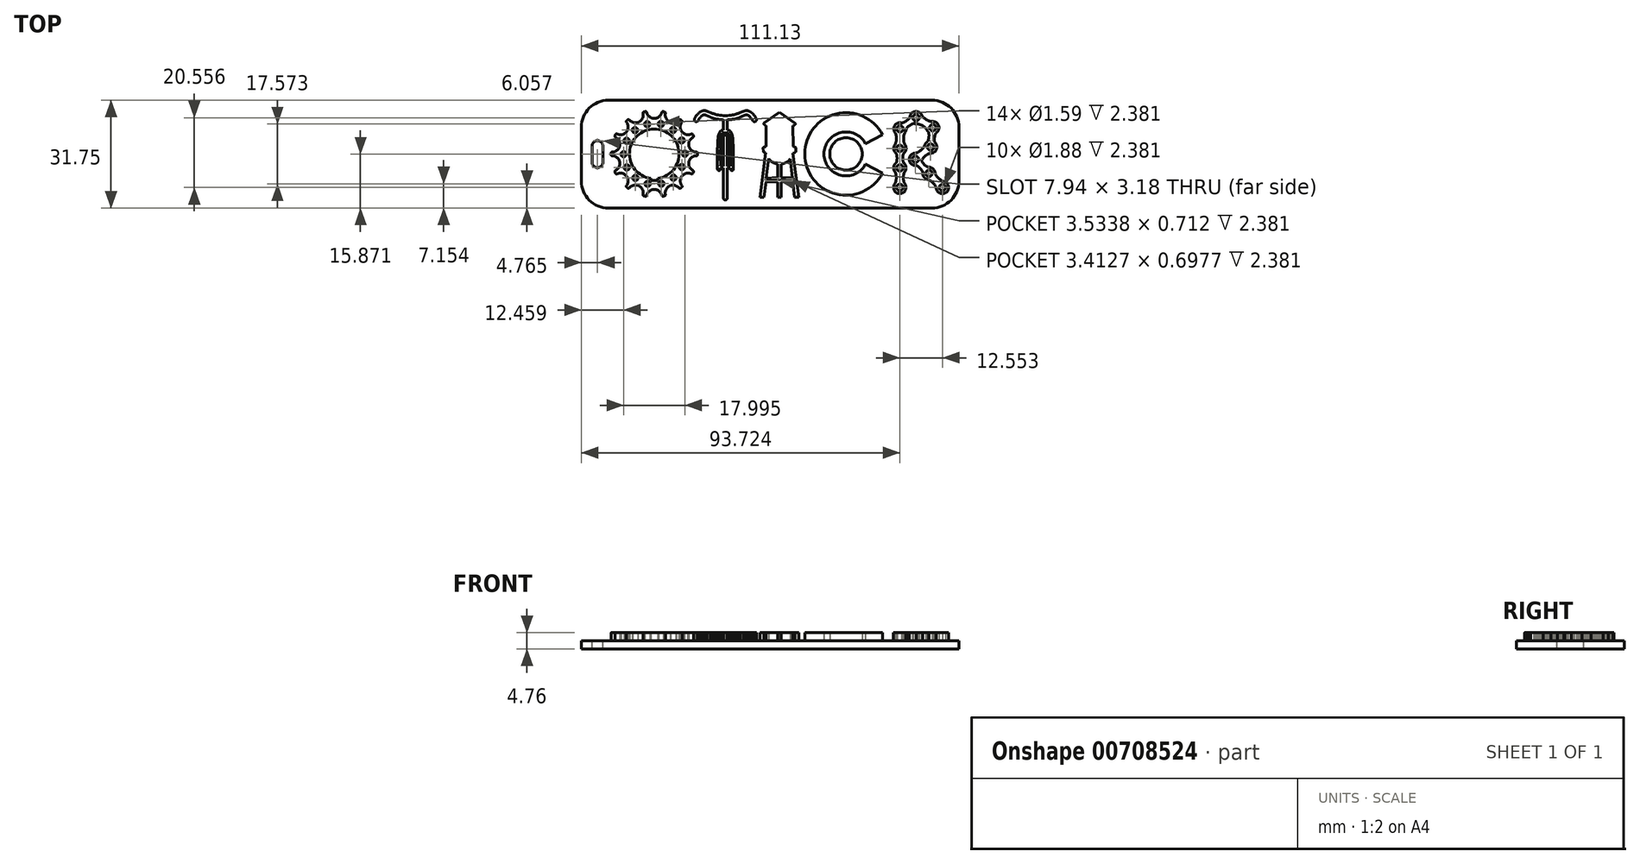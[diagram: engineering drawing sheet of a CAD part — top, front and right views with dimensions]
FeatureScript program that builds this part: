
annotation { "Feature Type Name" : "Feature", "Feature Type Description" : "" }
export const myFeature = defineFeature(function(context is Context, id is Id, definition is map)
    precondition{}
    {
        {
            var Q0;
            Q0=qCreatedBy(makeId("Top.planeOp"),FACE);
            var sketch = newSketch(context, id + "F0", { "sketchPlane" : qUnion([Q0])});
            skArc(sketch, "E0", {"start": v(-33.82, 12.73) * mm, "mid": v(-34.05, 12.78) * mm, "end": v(-34.28, 12.83) * mm});
            skArc(sketch, "E1", {"start": v(-33.6, 12.35) * mm, "mid": v(-33.63, 12.59) * mm, "end": v(-33.82, 12.73) * mm});
            skArc(sketch, "E2", {"start": v(-39.1, 12.6) * mm, "mid": v(-36.88, 10.82) * mm, "end": v(-34.66, 12.6) * mm});
            skArc(sketch, "E3", {"start": v(-34.28, 12.83) * mm, "mid": v(-34.52, 12.8) * mm, "end": v(-34.66, 12.6) * mm});
            skArc(sketch, "E4", {"start": v(-39.48, 12.83) * mm, "mid": v(-39.71, 12.78) * mm, "end": v(-39.94, 12.73) * mm});
            skArc(sketch, "E5", {"start": v(-39.1, 12.6) * mm, "mid": v(-39.25, 12.8) * mm, "end": v(-39.48, 12.83) * mm});
            skArc(sketch, "E6", {"start": v(-44.19, 10.42) * mm, "mid": v(-41.41, 9.79) * mm, "end": v(-40.18, 12.35) * mm});
            skArc(sketch, "E7", {"start": v(-39.94, 12.73) * mm, "mid": v(-40.14, 12.59) * mm, "end": v(-40.18, 12.35) * mm});
            skArc(sketch, "E8", {"start": v(-44.63, 10.47) * mm, "mid": v(-44.82, 10.33) * mm, "end": v(-45, 10.18) * mm});
            skArc(sketch, "E9", {"start": v(-44.19, 10.42) * mm, "mid": v(-44.4, 10.54) * mm, "end": v(-44.63, 10.47) * mm});
            skArc(sketch, "E10", {"start": v(-47.82, 6.26) * mm, "mid": v(-45.04, 6.89) * mm, "end": v(-45.04, 9.74) * mm});
            skArc(sketch, "E11", {"start": v(-45, 10.18) * mm, "mid": v(-45.11, 9.97) * mm, "end": v(-45.04, 9.74) * mm});
            skArc(sketch, "E12", {"start": v(-48.24, 6.11) * mm, "mid": v(-48.35, 5.9) * mm, "end": v(-48.45, 5.69) * mm});
            skArc(sketch, "E13", {"start": v(-47.82, 6.26) * mm, "mid": v(-48.06, 6.27) * mm, "end": v(-48.24, 6.11) * mm});
            skArc(sketch, "E14", {"start": v(-49.29, 0.93) * mm, "mid": v(-47.06, 2.7) * mm, "end": v(-48.3, 5.27) * mm});
            skArc(sketch, "E15", {"start": v(-48.45, 5.69) * mm, "mid": v(-48.46, 5.45) * mm, "end": v(-48.3, 5.27) * mm});
            skArc(sketch, "E16", {"start": v(-49.6, 0.62) * mm, "mid": v(-49.6, 0.38) * mm, "end": v(-49.6, 0.15) * mm});
            skArc(sketch, "E17", {"start": v(-49.29, 0.93) * mm, "mid": v(-49.5, 0.84) * mm, "end": v(-49.6, 0.62) * mm});
            skArc(sketch, "E18", {"start": v(-48.3, -4.5) * mm, "mid": v(-47.06, -1.94) * mm, "end": v(-49.29, -0.17) * mm});
            skArc(sketch, "E19", {"start": v(-49.6, 0.15) * mm, "mid": v(-49.5, -0.08) * mm, "end": v(-49.29, -0.17) * mm});
            skArc(sketch, "E20", {"start": v(-48.45, -4.93) * mm, "mid": v(-48.35, -5.14) * mm, "end": v(-48.24, -5.35) * mm});
            skArc(sketch, "E21", {"start": v(-48.3, -4.5) * mm, "mid": v(-48.46, -4.69) * mm, "end": v(-48.45, -4.93) * mm});
            skArc(sketch, "E22", {"start": v(-45.04, -8.97) * mm, "mid": v(-45.04, -6.13) * mm, "end": v(-47.82, -5.5) * mm});
            skArc(sketch, "E23", {"start": v(-48.24, -5.35) * mm, "mid": v(-48.06, -5.5) * mm, "end": v(-47.82, -5.5) * mm});
            skArc(sketch, "E24", {"start": v(-45, -9.42) * mm, "mid": v(-44.82, -9.57) * mm, "end": v(-44.63, -9.71) * mm});
            skArc(sketch, "E25", {"start": v(-45.04, -8.97) * mm, "mid": v(-45.11, -9.2) * mm, "end": v(-45, -9.42) * mm});
            skArc(sketch, "E26", {"start": v(-40.18, -11.59) * mm, "mid": v(-41.41, -9.02) * mm, "end": v(-44.19, -9.66) * mm});
            skArc(sketch, "E27", {"start": v(-44.63, -9.71) * mm, "mid": v(-44.4, -9.77) * mm, "end": v(-44.19, -9.66) * mm});
            skArc(sketch, "E28", {"start": v(-39.94, -11.97) * mm, "mid": v(-39.71, -12.02) * mm, "end": v(-39.48, -12.07) * mm});
            skArc(sketch, "E29", {"start": v(-40.18, -11.59) * mm, "mid": v(-40.14, -11.83) * mm, "end": v(-39.94, -11.97) * mm});
            skArc(sketch, "E30", {"start": v(-34.66, -11.83) * mm, "mid": v(-36.88, -10.06) * mm, "end": v(-39.1, -11.83) * mm});
            skArc(sketch, "E31", {"start": v(-39.48, -12.07) * mm, "mid": v(-39.25, -12.03) * mm, "end": v(-39.1, -11.83) * mm});
            skArc(sketch, "E32", {"start": v(-34.28, -12.07) * mm, "mid": v(-34.05, -12.02) * mm, "end": v(-33.82, -11.97) * mm});
            skArc(sketch, "E33", {"start": v(-34.66, -11.83) * mm, "mid": v(-34.52, -12.03) * mm, "end": v(-34.28, -12.07) * mm});
            skArc(sketch, "E34", {"start": v(-29.58, -9.66) * mm, "mid": v(-32.35, -9.02) * mm, "end": v(-33.6, -11.59) * mm});
            skArc(sketch, "E35", {"start": v(-33.82, -11.97) * mm, "mid": v(-33.63, -11.83) * mm, "end": v(-33.6, -11.59) * mm});
            skArc(sketch, "E36", {"start": v(-29.14, -9.71) * mm, "mid": v(-28.95, -9.57) * mm, "end": v(-28.77, -9.42) * mm});
            skArc(sketch, "E37", {"start": v(-29.58, -9.66) * mm, "mid": v(-29.37, -9.77) * mm, "end": v(-29.14, -9.71) * mm});
            skArc(sketch, "E38", {"start": v(-25.95, -5.5) * mm, "mid": v(-28.72, -6.13) * mm, "end": v(-28.72, -8.97) * mm});
            skArc(sketch, "E39", {"start": v(-28.77, -9.42) * mm, "mid": v(-28.66, -9.2) * mm, "end": v(-28.72, -8.97) * mm});
            skArc(sketch, "E40", {"start": v(-25.52, -5.35) * mm, "mid": v(-25.42, -5.14) * mm, "end": v(-25.32, -4.93) * mm});
            skArc(sketch, "E41", {"start": v(-25.95, -5.5) * mm, "mid": v(-25.7, -5.5) * mm, "end": v(-25.52, -5.35) * mm});
            skArc(sketch, "E42", {"start": v(-24.48, -0.17) * mm, "mid": v(-26.7, -1.94) * mm, "end": v(-25.47, -4.5) * mm});
            skArc(sketch, "E43", {"start": v(-25.32, -4.93) * mm, "mid": v(-25.31, -4.69) * mm, "end": v(-25.47, -4.5) * mm});
            skArc(sketch, "E44", {"start": v(-24.16, 0.15) * mm, "mid": v(-24.16, 0.38) * mm, "end": v(-24.16, 0.62) * mm});
            skArc(sketch, "E45", {"start": v(-24.48, -0.17) * mm, "mid": v(-24.26, -0.08) * mm, "end": v(-24.16, 0.15) * mm});
            skArc(sketch, "E46", {"start": v(-25.47, 5.27) * mm, "mid": v(-26.7, 2.7) * mm, "end": v(-24.48, 0.93) * mm});
            skArc(sketch, "E47", {"start": v(-24.16, 0.62) * mm, "mid": v(-24.26, 0.84) * mm, "end": v(-24.48, 0.93) * mm});
            skArc(sketch, "E48", {"start": v(-25.32, 5.69) * mm, "mid": v(-25.42, 5.9) * mm, "end": v(-25.52, 6.11) * mm});
            skArc(sketch, "E49", {"start": v(-25.47, 5.27) * mm, "mid": v(-25.31, 5.45) * mm, "end": v(-25.32, 5.69) * mm});
            skArc(sketch, "E50", {"start": v(-28.72, 9.74) * mm, "mid": v(-28.72, 6.89) * mm, "end": v(-25.95, 6.26) * mm});
            skArc(sketch, "E51", {"start": v(-25.52, 6.11) * mm, "mid": v(-25.7, 6.27) * mm, "end": v(-25.95, 6.26) * mm});
            skArc(sketch, "E52", {"start": v(-28.77, 10.18) * mm, "mid": v(-28.95, 10.33) * mm, "end": v(-29.14, 10.47) * mm});
            skArc(sketch, "E53", {"start": v(-28.72, 9.74) * mm, "mid": v(-28.66, 9.97) * mm, "end": v(-28.77, 10.18) * mm});
            skArc(sketch, "E54", {"start": v(-33.6, 12.35) * mm, "mid": v(-32.35, 9.79) * mm, "end": v(-29.58, 10.42) * mm});
            skArc(sketch, "E55", {"start": v(-29.14, 10.47) * mm, "mid": v(-29.37, 10.54) * mm, "end": v(-29.58, 10.42) * mm});
            skArc(sketch, "E56", {"start": v(-35.84, -6.84) * mm, "mid": v(-36.88, 7.68) * mm, "end": v(-37.93, -6.84) * mm});
            skCircle(sketch, "E57", {"center": v(19.55, 0.38) * mm, "radius": 4.78 * mm});
            skLineSegment(sketch, "E58", {"start": v(25.28, 3.4) * mm, "end": v(30.31, 6.04) * mm});
            skArc(sketch, "E59", {"start": v(30.31, 6.04) * mm, "mid": v(7.4, 0.38) * mm, "end": v(30.31, -5.28) * mm});
            skLineSegment(sketch, "E60", {"start": v(25.28, -2.63) * mm, "end": v(30.31, -5.28) * mm});
            skLineSegment(sketch, "E61", {"start": v(5.68, -12.44) * mm, "end": v(3.96, 0.55) * mm});
            skLineSegment(sketch, "E62", {"start": v(4.46, -12.44) * mm, "end": v(3.92, -7.7) * mm});
            skLineSegment(sketch, "E63", {"start": v(3.84, -7.32) * mm, "end": v(3.8, -7) * mm});
            skLineSegment(sketch, "E64", {"start": v(3.8, -6.65) * mm, "end": v(3.17, -1.11) * mm});
            skLineSegment(sketch, "E65", {"start": v(-0.06, 12.66) * mm, "end": v(4.72, 9.38) * mm});
            skLineSegment(sketch, "E66", {"start": v(-4.57, 9.45) * mm, "end": v(-0.06, 12.66) * mm});
            skLineSegment(sketch, "E67", {"start": v(3.92, -7.7) * mm, "end": v(0.42, -7.91) * mm});
            skLineSegment(sketch, "E68", {"start": v(-0.52, -7.9) * mm, "end": v(-4.03, -7.78) * mm});
            skLineSegment(sketch, "E69", {"start": v(-3.93, -6.74) * mm, "end": v(-0.52, -6.5) * mm});
            skLineSegment(sketch, "E70", {"start": v(0.42, -6.52) * mm, "end": v(3.8, -6.65) * mm});
            skLineSegment(sketch, "E71", {"start": v(3.84, -7.32) * mm, "end": v(0.42, -7.6) * mm});
            skLineSegment(sketch, "E72", {"start": v(-0.52, -7.54) * mm, "end": v(-4.05, -7.42) * mm});
            skLineSegment(sketch, "E73", {"start": v(-4.05, -7.42) * mm, "end": v(-3.98, -7.09) * mm});
            skLineSegment(sketch, "E74", {"start": v(-3.98, -7.09) * mm, "end": v(-0.52, -6.83) * mm});
            skLineSegment(sketch, "E75", {"start": v(0.42, -6.9) * mm, "end": v(3.8, -7) * mm});
            skLineSegment(sketch, "E76", {"start": v(3.94, 8.66) * mm, "end": v(4.02, 2.56) * mm});
            skLineSegment(sketch, "E77", {"start": v(-3.97, 8.65) * mm, "end": v(-3.96, 2.58) * mm});
            skLineSegment(sketch, "E78", {"start": v(4.85, 2.2) * mm, "end": v(4.82, 1.03) * mm});
            skLineSegment(sketch, "E79", {"start": v(-4.82, 2.22) * mm, "end": v(-4.8, 1) * mm});
            skArc(sketch, "E80", {"start": v(3.94, 8.66) * mm, "mid": v(4.44, 8.9) * mm, "end": v(4.72, 9.38) * mm});
            skArc(sketch, "E81", {"start": v(-4.57, 9.45) * mm, "mid": v(-4.44, 8.92) * mm, "end": v(-3.97, 8.65) * mm});
            skArc(sketch, "E82", {"start": v(4.85, 2.2) * mm, "mid": v(4.45, 2.43) * mm, "end": v(4.02, 2.56) * mm});
            skArc(sketch, "E83", {"start": v(-3.96, 2.58) * mm, "mid": v(-4.4, 2.44) * mm, "end": v(-4.82, 2.22) * mm});
            skArc(sketch, "E84", {"start": v(-4.8, 1) * mm, "mid": v(-4.43, 0.83) * mm, "end": v(-4.05, 0.7) * mm});
            skArc(sketch, "E85", {"start": v(3.96, 0.55) * mm, "mid": v(4.42, 0.74) * mm, "end": v(4.82, 1.03) * mm});
            skArc(sketch, "E86", {"start": v(-3.27, -0.99) * mm, "mid": v(-2.06, -2.07) * mm, "end": v(-0.52, -2.6) * mm});
            skArc(sketch, "E87", {"start": v(0.42, -2.6) * mm, "mid": v(1.94, -2.13) * mm, "end": v(3.17, -1.11) * mm});
            skLineSegment(sketch, "E88", {"start": v(-5.8, -12.44) * mm, "end": v(-4.05, 0.7) * mm});
            skLineSegment(sketch, "E89", {"start": v(-3.93, -6.74) * mm, "end": v(-3.27, -0.99) * mm});
            skLineSegment(sketch, "E90", {"start": v(-4.56, -12.44) * mm, "end": v(-4.03, -7.78) * mm});
            skLineSegment(sketch, "E91", {"start": v(-0.52, -2.6) * mm, "end": v(-0.52, -6.5) * mm});
            skLineSegment(sketch, "E92", {"start": v(-0.52, -7.9) * mm, "end": v(-0.52, -12.44) * mm});
            skLineSegment(sketch, "E93", {"start": v(0.42, -2.6) * mm, "end": v(0.42, -6.52) * mm});
            skLineSegment(sketch, "E94", {"start": v(0.42, -7.91) * mm, "end": v(0.42, -12.44) * mm});
            skLineSegment(sketch, "E95", {"start": v(-4.56, -12.44) * mm, "end": v(-5.8, -12.44) * mm});
            skLineSegment(sketch, "E96", {"start": v(0.42, -12.44) * mm, "end": v(-0.52, -12.44) * mm});
            skLineSegment(sketch, "E97", {"start": v(5.68, -12.44) * mm, "end": v(4.46, -12.44) * mm});
            skLineSegment(sketch, "E98", {"start": v(-15.95, 11.62) * mm, "end": v(-16.55, 11.66) * mm});
            skLineSegment(sketch, "E99", {"start": v(-16.55, 11.66) * mm, "end": v(-17.09, 11.7) * mm});
            skLineSegment(sketch, "E100", {"start": v(-17.09, 11.7) * mm, "end": v(-17.58, 11.77) * mm});
            skLineSegment(sketch, "E101", {"start": v(-17.58, 11.77) * mm, "end": v(-18.03, 11.84) * mm});
            skLineSegment(sketch, "E102", {"start": v(-18.03, 11.84) * mm, "end": v(-18.44, 11.93) * mm});
            skLineSegment(sketch, "E103", {"start": v(-18.44, 11.93) * mm, "end": v(-18.8, 12.02) * mm});
            skLineSegment(sketch, "E104", {"start": v(-18.8, 12.02) * mm, "end": v(-19.14, 12.1) * mm});
            skLineSegment(sketch, "E105", {"start": v(-19.14, 12.1) * mm, "end": v(-19.45, 12.2) * mm});
            skLineSegment(sketch, "E106", {"start": v(-19.45, 12.2) * mm, "end": v(-19.73, 12.3) * mm});
            skLineSegment(sketch, "E107", {"start": v(-19.73, 12.3) * mm, "end": v(-19.98, 12.39) * mm});
            skLineSegment(sketch, "E108", {"start": v(-19.98, 12.39) * mm, "end": v(-20.22, 12.48) * mm});
            skLineSegment(sketch, "E109", {"start": v(-20.22, 12.48) * mm, "end": v(-20.43, 12.56) * mm});
            skLineSegment(sketch, "E110", {"start": v(-20.43, 12.56) * mm, "end": v(-20.62, 12.64) * mm});
            skLineSegment(sketch, "E111", {"start": v(-20.62, 12.64) * mm, "end": v(-20.79, 12.72) * mm});
            skLineSegment(sketch, "E112", {"start": v(-20.79, 12.72) * mm, "end": v(-20.94, 12.78) * mm});
            skLineSegment(sketch, "E113", {"start": v(-20.94, 12.78) * mm, "end": v(-21.08, 12.85) * mm});
            skLineSegment(sketch, "E114", {"start": v(-21.08, 12.85) * mm, "end": v(-21.2, 12.9) * mm});
            skLineSegment(sketch, "E115", {"start": v(-21.2, 12.9) * mm, "end": v(-21.32, 12.95) * mm});
            skLineSegment(sketch, "E116", {"start": v(-21.32, 12.95) * mm, "end": v(-21.43, 12.98) * mm});
            skLineSegment(sketch, "E117", {"start": v(-21.43, 12.98) * mm, "end": v(-21.52, 13.02) * mm});
            skLineSegment(sketch, "E118", {"start": v(-21.52, 13.02) * mm, "end": v(-21.61, 13.05) * mm});
            skLineSegment(sketch, "E119", {"start": v(-21.61, 13.05) * mm, "end": v(-21.7, 13.07) * mm});
            skLineSegment(sketch, "E120", {"start": v(-21.7, 13.07) * mm, "end": v(-21.77, 13.09) * mm});
            skLineSegment(sketch, "E121", {"start": v(-21.77, 13.09) * mm, "end": v(-21.85, 13.1) * mm});
            skLineSegment(sketch, "E122", {"start": v(-21.85, 13.1) * mm, "end": v(-21.93, 13.11) * mm});
            skLineSegment(sketch, "E123", {"start": v(-21.93, 13.11) * mm, "end": v(-22, 13.12) * mm});
            skLineSegment(sketch, "E124", {"start": v(-22, 13.12) * mm, "end": v(-22.08, 13.13) * mm});
            skLineSegment(sketch, "E125", {"start": v(-22.08, 13.13) * mm, "end": v(-22.15, 13.13) * mm});
            skLineSegment(sketch, "E126", {"start": v(-22.15, 13.13) * mm, "end": v(-22.23, 13.13) * mm});
            skLineSegment(sketch, "E127", {"start": v(-22.23, 13.13) * mm, "end": v(-22.3, 13.12) * mm});
            skLineSegment(sketch, "E128", {"start": v(-22.3, 13.12) * mm, "end": v(-22.38, 13.11) * mm});
            skLineSegment(sketch, "E129", {"start": v(-22.38, 13.11) * mm, "end": v(-22.46, 13.1) * mm});
            skLineSegment(sketch, "E130", {"start": v(-22.46, 13.1) * mm, "end": v(-22.54, 13.09) * mm});
            skLineSegment(sketch, "E131", {"start": v(-22.54, 13.09) * mm, "end": v(-22.63, 13.07) * mm});
            skLineSegment(sketch, "E132", {"start": v(-22.63, 13.07) * mm, "end": v(-22.7, 13.04) * mm});
            skLineSegment(sketch, "E133", {"start": v(-22.7, 13.04) * mm, "end": v(-22.8, 13.02) * mm});
            skLineSegment(sketch, "E134", {"start": v(-22.8, 13.02) * mm, "end": v(-22.88, 12.99) * mm});
            skLineSegment(sketch, "E135", {"start": v(-22.88, 12.99) * mm, "end": v(-22.97, 12.95) * mm});
            skLineSegment(sketch, "E136", {"start": v(-22.97, 12.95) * mm, "end": v(-23.05, 12.91) * mm});
            skLineSegment(sketch, "E137", {"start": v(-23.05, 12.91) * mm, "end": v(-23.14, 12.87) * mm});
            skLineSegment(sketch, "E138", {"start": v(-23.14, 12.87) * mm, "end": v(-23.23, 12.82) * mm});
            skLineSegment(sketch, "E139", {"start": v(-23.23, 12.82) * mm, "end": v(-23.31, 12.77) * mm});
            skLineSegment(sketch, "E140", {"start": v(-23.31, 12.77) * mm, "end": v(-23.4, 12.72) * mm});
            skLineSegment(sketch, "E141", {"start": v(-23.4, 12.72) * mm, "end": v(-23.48, 12.66) * mm});
            skLineSegment(sketch, "E142", {"start": v(-23.48, 12.66) * mm, "end": v(-23.57, 12.6) * mm});
            skLineSegment(sketch, "E143", {"start": v(-23.57, 12.6) * mm, "end": v(-23.65, 12.53) * mm});
            skLineSegment(sketch, "E144", {"start": v(-23.65, 12.53) * mm, "end": v(-23.73, 12.47) * mm});
            skLineSegment(sketch, "E145", {"start": v(-23.73, 12.47) * mm, "end": v(-23.82, 12.4) * mm});
            skLineSegment(sketch, "E146", {"start": v(-23.82, 12.4) * mm, "end": v(-23.9, 12.32) * mm});
            skLineSegment(sketch, "E147", {"start": v(-23.9, 12.32) * mm, "end": v(-23.97, 12.25) * mm});
            skLineSegment(sketch, "E148", {"start": v(-23.97, 12.25) * mm, "end": v(-24.05, 12.17) * mm});
            skLineSegment(sketch, "E149", {"start": v(-24.05, 12.17) * mm, "end": v(-24.13, 12.08) * mm});
            skLineSegment(sketch, "E150", {"start": v(-24.13, 12.08) * mm, "end": v(-24.2, 12) * mm});
            skLineSegment(sketch, "E151", {"start": v(-24.2, 12) * mm, "end": v(-24.29, 11.9) * mm});
            skLineSegment(sketch, "E152", {"start": v(-24.29, 11.9) * mm, "end": v(-24.37, 11.8) * mm});
            skLineSegment(sketch, "E153", {"start": v(-24.37, 11.8) * mm, "end": v(-24.45, 11.69) * mm});
            skLineSegment(sketch, "E154", {"start": v(-24.45, 11.69) * mm, "end": v(-24.53, 11.57) * mm});
            skLineSegment(sketch, "E155", {"start": v(-24.53, 11.57) * mm, "end": v(-24.61, 11.45) * mm});
            skLineSegment(sketch, "E156", {"start": v(-24.61, 11.45) * mm, "end": v(-24.7, 11.33) * mm});
            skLineSegment(sketch, "E157", {"start": v(-24.7, 11.33) * mm, "end": v(-24.77, 11.2) * mm});
            skLineSegment(sketch, "E158", {"start": v(-24.77, 11.2) * mm, "end": v(-24.84, 11.08) * mm});
            skLineSegment(sketch, "E159", {"start": v(-24.84, 11.08) * mm, "end": v(-24.9, 10.96) * mm});
            skLineSegment(sketch, "E160", {"start": v(-24.9, 10.96) * mm, "end": v(-24.97, 10.85) * mm});
            skLineSegment(sketch, "E161", {"start": v(-24.97, 10.85) * mm, "end": v(-25.01, 10.74) * mm});
            skLineSegment(sketch, "E162", {"start": v(-25.01, 10.74) * mm, "end": v(-25.05, 10.65) * mm});
            skLineSegment(sketch, "E163", {"start": v(-25.05, 10.65) * mm, "end": v(-25.08, 10.57) * mm});
            skLineSegment(sketch, "E164", {"start": v(-25.08, 10.57) * mm, "end": v(-25.1, 10.5) * mm});
            skLineSegment(sketch, "E165", {"start": v(-25.1, 10.5) * mm, "end": v(-25.1, 10.43) * mm});
            skLineSegment(sketch, "E166", {"start": v(-25.1, 10.43) * mm, "end": v(-25.1, 10.38) * mm});
            skLineSegment(sketch, "E167", {"start": v(-25.1, 10.38) * mm, "end": v(-25.1, 10.32) * mm});
            skLineSegment(sketch, "E168", {"start": v(-25.1, 10.32) * mm, "end": v(-25.08, 10.27) * mm});
            skLineSegment(sketch, "E169", {"start": v(-25.08, 10.27) * mm, "end": v(-25.06, 10.23) * mm});
            skLineSegment(sketch, "E170", {"start": v(-25.06, 10.23) * mm, "end": v(-25.04, 10.18) * mm});
            skLineSegment(sketch, "E171", {"start": v(-25.04, 10.18) * mm, "end": v(-25, 10.14) * mm});
            skLineSegment(sketch, "E172", {"start": v(-25, 10.14) * mm, "end": v(-24.98, 10.1) * mm});
            skLineSegment(sketch, "E173", {"start": v(-24.98, 10.1) * mm, "end": v(-24.94, 10.06) * mm});
            skLineSegment(sketch, "E174", {"start": v(-24.94, 10.06) * mm, "end": v(-24.9, 10.03) * mm});
            skLineSegment(sketch, "E175", {"start": v(-24.9, 10.03) * mm, "end": v(-24.87, 10) * mm});
            skLineSegment(sketch, "E176", {"start": v(-24.87, 10) * mm, "end": v(-24.82, 9.97) * mm});
            skLineSegment(sketch, "E177", {"start": v(-24.82, 9.97) * mm, "end": v(-24.78, 9.94) * mm});
            skLineSegment(sketch, "E178", {"start": v(-24.78, 9.94) * mm, "end": v(-24.73, 9.92) * mm});
            skLineSegment(sketch, "E179", {"start": v(-24.73, 9.92) * mm, "end": v(-24.68, 9.9) * mm});
            skLineSegment(sketch, "E180", {"start": v(-24.68, 9.9) * mm, "end": v(-24.64, 9.9) * mm});
            skLineSegment(sketch, "E181", {"start": v(-24.64, 9.9) * mm, "end": v(-24.59, 9.89) * mm});
            skLineSegment(sketch, "E182", {"start": v(-24.59, 9.89) * mm, "end": v(-24.54, 9.89) * mm});
            skLineSegment(sketch, "E183", {"start": v(-24.54, 9.89) * mm, "end": v(-24.49, 9.89) * mm});
            skLineSegment(sketch, "E184", {"start": v(-24.49, 9.89) * mm, "end": v(-24.44, 9.89) * mm});
            skLineSegment(sketch, "E185", {"start": v(-24.44, 9.89) * mm, "end": v(-24.4, 9.9) * mm});
            skLineSegment(sketch, "E186", {"start": v(-24.4, 9.9) * mm, "end": v(-24.35, 9.9) * mm});
            skLineSegment(sketch, "E187", {"start": v(-24.35, 9.9) * mm, "end": v(-24.3, 9.92) * mm});
            skLineSegment(sketch, "E188", {"start": v(-24.3, 9.92) * mm, "end": v(-24.26, 9.94) * mm});
            skLineSegment(sketch, "E189", {"start": v(-24.26, 9.94) * mm, "end": v(-24.22, 9.96) * mm});
            skLineSegment(sketch, "E190", {"start": v(-24.22, 9.96) * mm, "end": v(-24.18, 9.99) * mm});
            skLineSegment(sketch, "E191", {"start": v(-24.18, 9.99) * mm, "end": v(-24.14, 10.02) * mm});
            skLineSegment(sketch, "E192", {"start": v(-24.14, 10.02) * mm, "end": v(-24.1, 10.06) * mm});
            skLineSegment(sketch, "E193", {"start": v(-24.1, 10.06) * mm, "end": v(-24.06, 10.1) * mm});
            skLineSegment(sketch, "E194", {"start": v(-24.06, 10.1) * mm, "end": v(-24.02, 10.16) * mm});
            skLineSegment(sketch, "E195", {"start": v(-24.02, 10.16) * mm, "end": v(-23.97, 10.22) * mm});
            skLineSegment(sketch, "E196", {"start": v(-23.97, 10.22) * mm, "end": v(-23.93, 10.28) * mm});
            skLineSegment(sketch, "E197", {"start": v(-23.93, 10.28) * mm, "end": v(-23.88, 10.35) * mm});
            skLineSegment(sketch, "E198", {"start": v(-23.88, 10.35) * mm, "end": v(-23.83, 10.43) * mm});
            skLineSegment(sketch, "E199", {"start": v(-23.83, 10.43) * mm, "end": v(-23.78, 10.5) * mm});
            skLineSegment(sketch, "E200", {"start": v(-23.78, 10.5) * mm, "end": v(-23.72, 10.59) * mm});
            skLineSegment(sketch, "E201", {"start": v(-23.72, 10.59) * mm, "end": v(-23.66, 10.67) * mm});
            skLineSegment(sketch, "E202", {"start": v(-23.66, 10.67) * mm, "end": v(-23.6, 10.76) * mm});
            skLineSegment(sketch, "E203", {"start": v(-23.6, 10.76) * mm, "end": v(-23.54, 10.86) * mm});
            skLineSegment(sketch, "E204", {"start": v(-23.54, 10.86) * mm, "end": v(-23.47, 10.95) * mm});
            skLineSegment(sketch, "E205", {"start": v(-23.47, 10.95) * mm, "end": v(-23.4, 11.04) * mm});
            skLineSegment(sketch, "E206", {"start": v(-23.4, 11.04) * mm, "end": v(-23.32, 11.13) * mm});
            skLineSegment(sketch, "E207", {"start": v(-23.32, 11.13) * mm, "end": v(-23.24, 11.22) * mm});
            skLineSegment(sketch, "E208", {"start": v(-23.24, 11.22) * mm, "end": v(-23.17, 11.3) * mm});
            skLineSegment(sketch, "E209", {"start": v(-23.17, 11.3) * mm, "end": v(-23.1, 11.39) * mm});
            skLineSegment(sketch, "E210", {"start": v(-23.1, 11.39) * mm, "end": v(-23.01, 11.46) * mm});
            skLineSegment(sketch, "E211", {"start": v(-23.01, 11.46) * mm, "end": v(-22.94, 11.53) * mm});
            skLineSegment(sketch, "E212", {"start": v(-22.94, 11.53) * mm, "end": v(-22.86, 11.6) * mm});
            skLineSegment(sketch, "E213", {"start": v(-22.86, 11.6) * mm, "end": v(-22.78, 11.65) * mm});
            skLineSegment(sketch, "E214", {"start": v(-22.78, 11.65) * mm, "end": v(-22.7, 11.7) * mm});
            skLineSegment(sketch, "E215", {"start": v(-22.7, 11.7) * mm, "end": v(-22.64, 11.75) * mm});
            skLineSegment(sketch, "E216", {"start": v(-22.64, 11.75) * mm, "end": v(-22.57, 11.79) * mm});
            skLineSegment(sketch, "E217", {"start": v(-22.57, 11.79) * mm, "end": v(-22.5, 11.82) * mm});
            skLineSegment(sketch, "E218", {"start": v(-22.5, 11.82) * mm, "end": v(-22.44, 11.85) * mm});
            skLineSegment(sketch, "E219", {"start": v(-22.44, 11.85) * mm, "end": v(-22.37, 11.87) * mm});
            skLineSegment(sketch, "E220", {"start": v(-22.37, 11.87) * mm, "end": v(-22.31, 11.88) * mm});
            skLineSegment(sketch, "E221", {"start": v(-22.31, 11.88) * mm, "end": v(-22.26, 11.9) * mm});
            skLineSegment(sketch, "E222", {"start": v(-22.26, 11.9) * mm, "end": v(-22.2, 11.9) * mm});
            skLineSegment(sketch, "E223", {"start": v(-22.2, 11.9) * mm, "end": v(-22.14, 11.9) * mm});
            skLineSegment(sketch, "E224", {"start": v(-22.14, 11.9) * mm, "end": v(-22.09, 11.9) * mm});
            skLineSegment(sketch, "E225", {"start": v(-22.09, 11.9) * mm, "end": v(-22.03, 11.89) * mm});
            skLineSegment(sketch, "E226", {"start": v(-22.03, 11.89) * mm, "end": v(-21.97, 11.88) * mm});
            skLineSegment(sketch, "E227", {"start": v(-21.97, 11.88) * mm, "end": v(-21.92, 11.87) * mm});
            skLineSegment(sketch, "E228", {"start": v(-21.92, 11.87) * mm, "end": v(-21.85, 11.85) * mm});
            skLineSegment(sketch, "E229", {"start": v(-21.85, 11.85) * mm, "end": v(-21.79, 11.83) * mm});
            skLineSegment(sketch, "E230", {"start": v(-21.79, 11.83) * mm, "end": v(-21.72, 11.81) * mm});
            skLineSegment(sketch, "E231", {"start": v(-21.72, 11.81) * mm, "end": v(-21.64, 11.78) * mm});
            skLineSegment(sketch, "E232", {"start": v(-21.64, 11.78) * mm, "end": v(-21.56, 11.75) * mm});
            skLineSegment(sketch, "E233", {"start": v(-21.56, 11.75) * mm, "end": v(-21.47, 11.7) * mm});
            skLineSegment(sketch, "E234", {"start": v(-21.47, 11.7) * mm, "end": v(-21.36, 11.66) * mm});
            skLineSegment(sketch, "E235", {"start": v(-21.36, 11.66) * mm, "end": v(-21.25, 11.61) * mm});
            skLineSegment(sketch, "E236", {"start": v(-21.25, 11.61) * mm, "end": v(-21.14, 11.56) * mm});
            skLineSegment(sketch, "E237", {"start": v(-21.14, 11.56) * mm, "end": v(-21.01, 11.5) * mm});
            skLineSegment(sketch, "E238", {"start": v(-21.01, 11.5) * mm, "end": v(-20.88, 11.44) * mm});
            skLineSegment(sketch, "E239", {"start": v(-20.88, 11.44) * mm, "end": v(-20.75, 11.38) * mm});
            skLineSegment(sketch, "E240", {"start": v(-20.75, 11.38) * mm, "end": v(-20.61, 11.31) * mm});
            skLineSegment(sketch, "E241", {"start": v(-20.61, 11.31) * mm, "end": v(-20.48, 11.25) * mm});
            skLineSegment(sketch, "E242", {"start": v(-20.48, 11.25) * mm, "end": v(-20.34, 11.2) * mm});
            skLineSegment(sketch, "E243", {"start": v(-20.34, 11.2) * mm, "end": v(-20.2, 11.13) * mm});
            skLineSegment(sketch, "E244", {"start": v(-20.2, 11.13) * mm, "end": v(-20.06, 11.08) * mm});
            skLineSegment(sketch, "E245", {"start": v(-20.06, 11.08) * mm, "end": v(-19.92, 11.02) * mm});
            skLineSegment(sketch, "E246", {"start": v(-19.92, 11.02) * mm, "end": v(-19.78, 10.97) * mm});
            skLineSegment(sketch, "E247", {"start": v(-19.78, 10.97) * mm, "end": v(-19.63, 10.92) * mm});
            skLineSegment(sketch, "E248", {"start": v(-19.63, 10.92) * mm, "end": v(-19.49, 10.87) * mm});
            skLineSegment(sketch, "E249", {"start": v(-19.49, 10.87) * mm, "end": v(-19.34, 10.82) * mm});
            skLineSegment(sketch, "E250", {"start": v(-19.34, 10.82) * mm, "end": v(-19.2, 10.78) * mm});
            skLineSegment(sketch, "E251", {"start": v(-19.2, 10.78) * mm, "end": v(-19.04, 10.74) * mm});
            skLineSegment(sketch, "E252", {"start": v(-19.04, 10.74) * mm, "end": v(-18.89, 10.7) * mm});
            skLineSegment(sketch, "E253", {"start": v(-18.89, 10.7) * mm, "end": v(-18.73, 10.67) * mm});
            skLineSegment(sketch, "E254", {"start": v(-18.73, 10.67) * mm, "end": v(-18.56, 10.64) * mm});
            skLineSegment(sketch, "E255", {"start": v(-18.56, 10.64) * mm, "end": v(-18.38, 10.6) * mm});
            skLineSegment(sketch, "E256", {"start": v(-18.38, 10.6) * mm, "end": v(-18.2, 10.58) * mm});
            skLineSegment(sketch, "E257", {"start": v(-18.2, 10.58) * mm, "end": v(-18, 10.55) * mm});
            skLineSegment(sketch, "E258", {"start": v(-18, 10.55) * mm, "end": v(-17.8, 10.52) * mm});
            skLineSegment(sketch, "E259", {"start": v(-17.8, 10.52) * mm, "end": v(-17.58, 10.5) * mm});
            skLineSegment(sketch, "E260", {"start": v(-17.58, 10.5) * mm, "end": v(-17.36, 10.48) * mm});
            skLineSegment(sketch, "E261", {"start": v(-17.36, 10.48) * mm, "end": v(-17.15, 10.46) * mm});
            skLineSegment(sketch, "E262", {"start": v(-17.15, 10.46) * mm, "end": v(-16.96, 10.44) * mm});
            skLineSegment(sketch, "E263", {"start": v(-16.96, 10.44) * mm, "end": v(-16.78, 10.43) * mm});
            skLineSegment(sketch, "E264", {"start": v(-16.78, 10.43) * mm, "end": v(-16.63, 10.42) * mm});
            skLineSegment(sketch, "E265", {"start": v(-16.63, 10.42) * mm, "end": v(-16.5, 10.42) * mm});
            skLineSegment(sketch, "E266", {"start": v(-16.5, -12.68) * mm, "end": v(-16.5, -3.7) * mm});
            skLineSegment(sketch, "E267", {"start": v(-16.5, -3.7) * mm, "end": v(-17.39, -3.7) * mm});
            skLineSegment(sketch, "E268", {"start": v(-17.39, -3.7) * mm, "end": v(-17.4, -3.85) * mm});
            skLineSegment(sketch, "E269", {"start": v(-17.4, -3.85) * mm, "end": v(-17.4, -4.05) * mm});
            skLineSegment(sketch, "E270", {"start": v(-17.4, -4.05) * mm, "end": v(-17.43, -4.19) * mm});
            skLineSegment(sketch, "E271", {"start": v(-17.43, -4.19) * mm, "end": v(-17.45, -4.29) * mm});
            skLineSegment(sketch, "E272", {"start": v(-17.45, -4.29) * mm, "end": v(-17.48, -4.35) * mm});
            skLineSegment(sketch, "E273", {"start": v(-17.48, -4.35) * mm, "end": v(-17.5, -4.39) * mm});
            skLineSegment(sketch, "E274", {"start": v(-17.5, -4.39) * mm, "end": v(-17.54, -4.41) * mm});
            skLineSegment(sketch, "E275", {"start": v(-17.54, -4.41) * mm, "end": v(-17.57, -4.43) * mm});
            skLineSegment(sketch, "E276", {"start": v(-17.57, -4.43) * mm, "end": v(-17.6, -4.45) * mm});
            skLineSegment(sketch, "E277", {"start": v(-17.6, -4.45) * mm, "end": v(-17.64, -4.47) * mm});
            skLineSegment(sketch, "E278", {"start": v(-17.64, -4.47) * mm, "end": v(-17.68, -4.48) * mm});
            skLineSegment(sketch, "E279", {"start": v(-17.68, -4.48) * mm, "end": v(-17.72, -4.5) * mm});
            skLineSegment(sketch, "E280", {"start": v(-17.72, -4.5) * mm, "end": v(-17.76, -4.5) * mm});
            skLineSegment(sketch, "E281", {"start": v(-17.76, -4.5) * mm, "end": v(-17.8, -4.5) * mm});
            skLineSegment(sketch, "E282", {"start": v(-17.8, -4.5) * mm, "end": v(-17.85, -4.5) * mm});
            skLineSegment(sketch, "E283", {"start": v(-17.85, -4.5) * mm, "end": v(-17.89, -4.5) * mm});
            skLineSegment(sketch, "E284", {"start": v(-17.89, -4.5) * mm, "end": v(-17.93, -4.5) * mm});
            skLineSegment(sketch, "E285", {"start": v(-17.93, -4.5) * mm, "end": v(-17.97, -4.48) * mm});
            skLineSegment(sketch, "E286", {"start": v(-17.97, -4.48) * mm, "end": v(-18.01, -4.47) * mm});
            skLineSegment(sketch, "E287", {"start": v(-18.01, -4.47) * mm, "end": v(-18.05, -4.46) * mm});
            skLineSegment(sketch, "E288", {"start": v(-18.05, -4.46) * mm, "end": v(-18.09, -4.44) * mm});
            skLineSegment(sketch, "E289", {"start": v(-18.09, -4.44) * mm, "end": v(-18.12, -4.42) * mm});
            skLineSegment(sketch, "E290", {"start": v(-18.12, -4.42) * mm, "end": v(-18.16, -4.4) * mm});
            skLineSegment(sketch, "E291", {"start": v(-18.16, -4.4) * mm, "end": v(-18.19, -4.37) * mm});
            skLineSegment(sketch, "E292", {"start": v(-18.19, -4.37) * mm, "end": v(-18.21, -4.34) * mm});
            skLineSegment(sketch, "E293", {"start": v(-18.21, -4.34) * mm, "end": v(-18.24, -4.28) * mm});
            skLineSegment(sketch, "E294", {"start": v(-18.24, -4.28) * mm, "end": v(-18.26, -4.2) * mm});
            skLineSegment(sketch, "E295", {"start": v(-18.26, -4.2) * mm, "end": v(-18.27, -4.1) * mm});
            skLineSegment(sketch, "E296", {"start": v(-18.27, -4.1) * mm, "end": v(-18.29, -3.94) * mm});
            skLineSegment(sketch, "E297", {"start": v(-18.29, -3.94) * mm, "end": v(-18.3, -3.74) * mm});
            skLineSegment(sketch, "E298", {"start": v(-18.3, -3.74) * mm, "end": v(-18.31, -3.48) * mm});
            skLineSegment(sketch, "E299", {"start": v(-18.31, -3.48) * mm, "end": v(-18.32, -3.16) * mm});
            skLineSegment(sketch, "E300", {"start": v(-18.32, -3.16) * mm, "end": v(-18.32, -2.79) * mm});
            skLineSegment(sketch, "E301", {"start": v(-18.32, -2.79) * mm, "end": v(-18.32, -2.36) * mm});
            skLineSegment(sketch, "E302", {"start": v(-18.32, -2.36) * mm, "end": v(-18.32, -1.9) * mm});
            skLineSegment(sketch, "E303", {"start": v(-18.32, -1.9) * mm, "end": v(-18.32, -1.4) * mm});
            skLineSegment(sketch, "E304", {"start": v(-18.32, -1.4) * mm, "end": v(-18.32, -0.87) * mm});
            skLineSegment(sketch, "E305", {"start": v(-18.32, -0.87) * mm, "end": v(-18.31, -0.33) * mm});
            skLineSegment(sketch, "E306", {"start": v(-18.31, -0.33) * mm, "end": v(-18.3, 0.23) * mm});
            skLineSegment(sketch, "E307", {"start": v(-18.3, 0.23) * mm, "end": v(-18.3, 0.8) * mm});
            skLineSegment(sketch, "E308", {"start": v(-18.3, 0.8) * mm, "end": v(-18.28, 1.35) * mm});
            skLineSegment(sketch, "E309", {"start": v(-18.28, 1.35) * mm, "end": v(-18.27, 1.9) * mm});
            skLineSegment(sketch, "E310", {"start": v(-18.27, 1.9) * mm, "end": v(-18.25, 2.45) * mm});
            skLineSegment(sketch, "E311", {"start": v(-18.25, 2.45) * mm, "end": v(-18.23, 2.97) * mm});
            skLineSegment(sketch, "E312", {"start": v(-18.23, 2.97) * mm, "end": v(-18.21, 3.46) * mm});
            skLineSegment(sketch, "E313", {"start": v(-18.21, 3.46) * mm, "end": v(-18.19, 3.92) * mm});
            skLineSegment(sketch, "E314", {"start": v(-18.19, 3.92) * mm, "end": v(-18.16, 4.35) * mm});
            skLineSegment(sketch, "E315", {"start": v(-18.16, 4.35) * mm, "end": v(-18.13, 4.73) * mm});
            skLineSegment(sketch, "E316", {"start": v(-18.13, 4.73) * mm, "end": v(-18.1, 5.07) * mm});
            skLineSegment(sketch, "E317", {"start": v(-18.1, 5.07) * mm, "end": v(-18.05, 5.37) * mm});
            skLineSegment(sketch, "E318", {"start": v(-18.05, 5.37) * mm, "end": v(-18.01, 5.64) * mm});
            skLineSegment(sketch, "E319", {"start": v(-18.01, 5.64) * mm, "end": v(-17.97, 5.87) * mm});
            skLineSegment(sketch, "E320", {"start": v(-17.97, 5.87) * mm, "end": v(-17.92, 6.08) * mm});
            skLineSegment(sketch, "E321", {"start": v(-17.92, 6.08) * mm, "end": v(-17.86, 6.27) * mm});
            skLineSegment(sketch, "E322", {"start": v(-17.86, 6.27) * mm, "end": v(-17.8, 6.43) * mm});
            skLineSegment(sketch, "E323", {"start": v(-17.8, 6.43) * mm, "end": v(-17.75, 6.58) * mm});
            skLineSegment(sketch, "E324", {"start": v(-17.75, 6.58) * mm, "end": v(-17.68, 6.7) * mm});
            skLineSegment(sketch, "E325", {"start": v(-17.68, 6.7) * mm, "end": v(-17.61, 6.82) * mm});
            skLineSegment(sketch, "E326", {"start": v(-17.61, 6.82) * mm, "end": v(-17.54, 6.93) * mm});
            skLineSegment(sketch, "E327", {"start": v(-17.54, 6.93) * mm, "end": v(-17.47, 7.02) * mm});
            skLineSegment(sketch, "E328", {"start": v(-17.47, 7.02) * mm, "end": v(-17.4, 7.1) * mm});
            skLineSegment(sketch, "E329", {"start": v(-17.4, 7.1) * mm, "end": v(-17.32, 7.16) * mm});
            skLineSegment(sketch, "E330", {"start": v(-17.32, 7.16) * mm, "end": v(-17.24, 7.22) * mm});
            skLineSegment(sketch, "E331", {"start": v(-17.24, 7.22) * mm, "end": v(-17.15, 7.28) * mm});
            skLineSegment(sketch, "E332", {"start": v(-17.15, 7.28) * mm, "end": v(-17.07, 7.32) * mm});
            skLineSegment(sketch, "E333", {"start": v(-17.07, 7.32) * mm, "end": v(-16.98, 7.36) * mm});
            skLineSegment(sketch, "E334", {"start": v(-16.98, 7.36) * mm, "end": v(-16.9, 7.4) * mm});
            skLineSegment(sketch, "E335", {"start": v(-16.9, 7.4) * mm, "end": v(-16.8, 7.42) * mm});
            skLineSegment(sketch, "E336", {"start": v(-16.8, 7.42) * mm, "end": v(-16.5, 7.48) * mm});
            skLineSegment(sketch, "E337", {"start": v(-16.5, 7.48) * mm, "end": v(-16.5, 10.42) * mm});
            skLineSegment(sketch, "E338", {"start": v(-16.16, 6.6) * mm, "end": v(-16.34, 6.6) * mm});
            skLineSegment(sketch, "E339", {"start": v(-16.34, 6.6) * mm, "end": v(-16.48, 6.59) * mm});
            skLineSegment(sketch, "E340", {"start": v(-16.48, 6.59) * mm, "end": v(-16.59, 6.57) * mm});
            skLineSegment(sketch, "E341", {"start": v(-16.59, 6.57) * mm, "end": v(-16.67, 6.55) * mm});
            skLineSegment(sketch, "E342", {"start": v(-16.67, 6.55) * mm, "end": v(-16.73, 6.53) * mm});
            skLineSegment(sketch, "E343", {"start": v(-16.73, 6.53) * mm, "end": v(-16.78, 6.5) * mm});
            skLineSegment(sketch, "E344", {"start": v(-16.78, 6.5) * mm, "end": v(-16.82, 6.47) * mm});
            skLineSegment(sketch, "E345", {"start": v(-16.82, 6.47) * mm, "end": v(-16.86, 6.44) * mm});
            skLineSegment(sketch, "E346", {"start": v(-16.86, 6.44) * mm, "end": v(-16.9, 6.4) * mm});
            skLineSegment(sketch, "E347", {"start": v(-16.9, 6.4) * mm, "end": v(-16.92, 6.37) * mm});
            skLineSegment(sketch, "E348", {"start": v(-16.92, 6.37) * mm, "end": v(-16.95, 6.32) * mm});
            skLineSegment(sketch, "E349", {"start": v(-16.95, 6.32) * mm, "end": v(-16.98, 6.27) * mm});
            skLineSegment(sketch, "E350", {"start": v(-16.98, 6.27) * mm, "end": v(-17, 6.22) * mm});
            skLineSegment(sketch, "E351", {"start": v(-17, 6.22) * mm, "end": v(-17.03, 6.16) * mm});
            skLineSegment(sketch, "E352", {"start": v(-17.03, 6.16) * mm, "end": v(-17.06, 6.1) * mm});
            skLineSegment(sketch, "E353", {"start": v(-17.06, 6.1) * mm, "end": v(-17.08, 6.01) * mm});
            skLineSegment(sketch, "E354", {"start": v(-17.08, 6.01) * mm, "end": v(-17.1, 5.93) * mm});
            skLineSegment(sketch, "E355", {"start": v(-17.1, 5.93) * mm, "end": v(-17.13, 5.82) * mm});
            skLineSegment(sketch, "E356", {"start": v(-17.13, 5.82) * mm, "end": v(-17.15, 5.7) * mm});
            skLineSegment(sketch, "E357", {"start": v(-17.15, 5.7) * mm, "end": v(-17.17, 5.54) * mm});
            skLineSegment(sketch, "E358", {"start": v(-17.17, 5.54) * mm, "end": v(-17.2, 5.35) * mm});
            skLineSegment(sketch, "E359", {"start": v(-17.2, 5.35) * mm, "end": v(-17.21, 5.13) * mm});
            skLineSegment(sketch, "E360", {"start": v(-17.21, 5.13) * mm, "end": v(-17.24, 4.87) * mm});
            skLineSegment(sketch, "E361", {"start": v(-17.24, 4.87) * mm, "end": v(-17.26, 4.57) * mm});
            skLineSegment(sketch, "E362", {"start": v(-17.26, 4.57) * mm, "end": v(-17.28, 4.22) * mm});
            skLineSegment(sketch, "E363", {"start": v(-17.28, 4.22) * mm, "end": v(-17.3, 3.83) * mm});
            skLineSegment(sketch, "E364", {"start": v(-17.3, 3.83) * mm, "end": v(-17.32, 3.4) * mm});
            skLineSegment(sketch, "E365", {"start": v(-17.32, 3.4) * mm, "end": v(-17.34, 2.93) * mm});
            skLineSegment(sketch, "E366", {"start": v(-17.34, 2.93) * mm, "end": v(-17.35, 2.42) * mm});
            skLineSegment(sketch, "E367", {"start": v(-17.35, 2.42) * mm, "end": v(-17.37, 1.88) * mm});
            skLineSegment(sketch, "E368", {"start": v(-17.37, 1.88) * mm, "end": v(-17.37, 1.3) * mm});
            skLineSegment(sketch, "E369", {"start": v(-17.37, 1.3) * mm, "end": v(-17.38, 0.7) * mm});
            skLineSegment(sketch, "E370", {"start": v(-17.38, 0.7) * mm, "end": v(-17.38, 0.07) * mm});
            skLineSegment(sketch, "E371", {"start": v(-17.38, 0.07) * mm, "end": v(-17.38, -0.57) * mm});
            skLineSegment(sketch, "E372", {"start": v(-17.38, -0.57) * mm, "end": v(-17.37, -1.18) * mm});
            skLineSegment(sketch, "E373", {"start": v(-17.37, -1.18) * mm, "end": v(-17.37, -1.78) * mm});
            skLineSegment(sketch, "E374", {"start": v(-17.37, -1.78) * mm, "end": v(-17.37, -2.33) * mm});
            skLineSegment(sketch, "E375", {"start": v(-17.37, -2.33) * mm, "end": v(-17.37, -2.82) * mm});
            skLineSegment(sketch, "E376", {"start": v(-17.37, -2.82) * mm, "end": v(-17.37, -3.28) * mm});
            skArc(sketch, "E377", {"start": v(-16.5, -12.68) * mm, "mid": v(-16.37, -13) * mm, "end": v(-16.06, -13.13) * mm});
            skLineSegment(sketch, "E378", {"start": v(-15.95, -13.13) * mm, "end": v(-16.06, -13.13) * mm});
            skArc(sketch, "E379", {"start": v(-16.06, 5.92) * mm, "mid": v(-16.37, 5.8) * mm, "end": v(-16.5, 5.48) * mm});
            skLineSegment(sketch, "E380", {"start": v(-16.5, -3.28) * mm, "end": v(-16.5, 5.48) * mm});
            skLineSegment(sketch, "E381", {"start": v(-15.95, 11.62) * mm, "end": v(-15.35, 11.66) * mm});
            skLineSegment(sketch, "E382", {"start": v(-15.35, 11.66) * mm, "end": v(-14.81, 11.7) * mm});
            skLineSegment(sketch, "E383", {"start": v(-14.81, 11.7) * mm, "end": v(-14.32, 11.77) * mm});
            skLineSegment(sketch, "E384", {"start": v(-14.32, 11.77) * mm, "end": v(-13.87, 11.84) * mm});
            skLineSegment(sketch, "E385", {"start": v(-13.87, 11.84) * mm, "end": v(-13.46, 11.93) * mm});
            skLineSegment(sketch, "E386", {"start": v(-13.46, 11.93) * mm, "end": v(-13.1, 12.02) * mm});
            skLineSegment(sketch, "E387", {"start": v(-13.1, 12.02) * mm, "end": v(-12.76, 12.1) * mm});
            skLineSegment(sketch, "E388", {"start": v(-12.76, 12.1) * mm, "end": v(-12.45, 12.2) * mm});
            skLineSegment(sketch, "E389", {"start": v(-12.45, 12.2) * mm, "end": v(-12.17, 12.3) * mm});
            skLineSegment(sketch, "E390", {"start": v(-12.17, 12.3) * mm, "end": v(-11.92, 12.39) * mm});
            skLineSegment(sketch, "E391", {"start": v(-11.92, 12.39) * mm, "end": v(-11.68, 12.48) * mm});
            skLineSegment(sketch, "E392", {"start": v(-11.68, 12.48) * mm, "end": v(-11.47, 12.56) * mm});
            skLineSegment(sketch, "E393", {"start": v(-11.47, 12.56) * mm, "end": v(-11.28, 12.64) * mm});
            skLineSegment(sketch, "E394", {"start": v(-11.28, 12.64) * mm, "end": v(-11.11, 12.72) * mm});
            skLineSegment(sketch, "E395", {"start": v(-11.11, 12.72) * mm, "end": v(-10.96, 12.78) * mm});
            skLineSegment(sketch, "E396", {"start": v(-10.96, 12.78) * mm, "end": v(-10.82, 12.85) * mm});
            skLineSegment(sketch, "E397", {"start": v(-10.82, 12.85) * mm, "end": v(-10.7, 12.9) * mm});
            skLineSegment(sketch, "E398", {"start": v(-10.7, 12.9) * mm, "end": v(-10.58, 12.95) * mm});
            skLineSegment(sketch, "E399", {"start": v(-10.58, 12.95) * mm, "end": v(-10.47, 12.98) * mm});
            skLineSegment(sketch, "E400", {"start": v(-10.47, 12.98) * mm, "end": v(-10.38, 13.02) * mm});
            skLineSegment(sketch, "E401", {"start": v(-10.38, 13.02) * mm, "end": v(-10.29, 13.05) * mm});
            skLineSegment(sketch, "E402", {"start": v(-10.29, 13.05) * mm, "end": v(-10.2, 13.07) * mm});
            skLineSegment(sketch, "E403", {"start": v(-10.2, 13.07) * mm, "end": v(-10.13, 13.09) * mm});
            skLineSegment(sketch, "E404", {"start": v(-10.13, 13.09) * mm, "end": v(-10.05, 13.1) * mm});
            skLineSegment(sketch, "E405", {"start": v(-10.05, 13.1) * mm, "end": v(-9.97, 13.11) * mm});
            skLineSegment(sketch, "E406", {"start": v(-9.97, 13.11) * mm, "end": v(-9.9, 13.12) * mm});
            skLineSegment(sketch, "E407", {"start": v(-9.9, 13.12) * mm, "end": v(-9.82, 13.13) * mm});
            skLineSegment(sketch, "E408", {"start": v(-9.82, 13.13) * mm, "end": v(-9.75, 13.13) * mm});
            skLineSegment(sketch, "E409", {"start": v(-9.75, 13.13) * mm, "end": v(-9.67, 13.13) * mm});
            skLineSegment(sketch, "E410", {"start": v(-9.67, 13.13) * mm, "end": v(-9.6, 13.12) * mm});
            skLineSegment(sketch, "E411", {"start": v(-9.6, 13.12) * mm, "end": v(-9.52, 13.11) * mm});
            skLineSegment(sketch, "E412", {"start": v(-9.52, 13.11) * mm, "end": v(-9.44, 13.1) * mm});
            skLineSegment(sketch, "E413", {"start": v(-9.44, 13.1) * mm, "end": v(-9.36, 13.09) * mm});
            skLineSegment(sketch, "E414", {"start": v(-9.36, 13.09) * mm, "end": v(-9.27, 13.07) * mm});
            skLineSegment(sketch, "E415", {"start": v(-9.27, 13.07) * mm, "end": v(-9.2, 13.04) * mm});
            skLineSegment(sketch, "E416", {"start": v(-9.2, 13.04) * mm, "end": v(-9.1, 13.02) * mm});
            skLineSegment(sketch, "E417", {"start": v(-9.1, 13.02) * mm, "end": v(-9.02, 12.99) * mm});
            skLineSegment(sketch, "E418", {"start": v(-9.02, 12.99) * mm, "end": v(-8.93, 12.95) * mm});
            skLineSegment(sketch, "E419", {"start": v(-8.93, 12.95) * mm, "end": v(-8.85, 12.91) * mm});
            skLineSegment(sketch, "E420", {"start": v(-8.85, 12.91) * mm, "end": v(-8.76, 12.87) * mm});
            skLineSegment(sketch, "E421", {"start": v(-8.76, 12.87) * mm, "end": v(-8.68, 12.82) * mm});
            skLineSegment(sketch, "E422", {"start": v(-8.68, 12.82) * mm, "end": v(-8.59, 12.77) * mm});
            skLineSegment(sketch, "E423", {"start": v(-8.59, 12.77) * mm, "end": v(-8.5, 12.72) * mm});
            skLineSegment(sketch, "E424", {"start": v(-8.5, 12.72) * mm, "end": v(-8.42, 12.66) * mm});
            skLineSegment(sketch, "E425", {"start": v(-8.42, 12.66) * mm, "end": v(-8.33, 12.6) * mm});
            skLineSegment(sketch, "E426", {"start": v(-8.33, 12.6) * mm, "end": v(-8.25, 12.53) * mm});
            skLineSegment(sketch, "E427", {"start": v(-8.25, 12.53) * mm, "end": v(-8.17, 12.47) * mm});
            skLineSegment(sketch, "E428", {"start": v(-8.17, 12.47) * mm, "end": v(-8.08, 12.4) * mm});
            skLineSegment(sketch, "E429", {"start": v(-8.08, 12.4) * mm, "end": v(-8, 12.32) * mm});
            skLineSegment(sketch, "E430", {"start": v(-8, 12.32) * mm, "end": v(-7.93, 12.25) * mm});
            skLineSegment(sketch, "E431", {"start": v(-7.93, 12.25) * mm, "end": v(-7.85, 12.17) * mm});
            skLineSegment(sketch, "E432", {"start": v(-7.85, 12.17) * mm, "end": v(-7.77, 12.08) * mm});
            skLineSegment(sketch, "E433", {"start": v(-7.77, 12.08) * mm, "end": v(-7.7, 12) * mm});
            skLineSegment(sketch, "E434", {"start": v(-7.7, 12) * mm, "end": v(-7.61, 11.9) * mm});
            skLineSegment(sketch, "E435", {"start": v(-7.61, 11.9) * mm, "end": v(-7.53, 11.8) * mm});
            skLineSegment(sketch, "E436", {"start": v(-7.53, 11.8) * mm, "end": v(-7.45, 11.69) * mm});
            skLineSegment(sketch, "E437", {"start": v(-7.45, 11.69) * mm, "end": v(-7.37, 11.57) * mm});
            skLineSegment(sketch, "E438", {"start": v(-7.37, 11.57) * mm, "end": v(-7.29, 11.45) * mm});
            skLineSegment(sketch, "E439", {"start": v(-7.29, 11.45) * mm, "end": v(-7.2, 11.33) * mm});
            skLineSegment(sketch, "E440", {"start": v(-7.2, 11.33) * mm, "end": v(-7.13, 11.2) * mm});
            skLineSegment(sketch, "E441", {"start": v(-7.13, 11.2) * mm, "end": v(-7.06, 11.08) * mm});
            skLineSegment(sketch, "E442", {"start": v(-7.06, 11.08) * mm, "end": v(-7, 10.96) * mm});
            skLineSegment(sketch, "E443", {"start": v(-7, 10.96) * mm, "end": v(-6.93, 10.85) * mm});
            skLineSegment(sketch, "E444", {"start": v(-6.93, 10.85) * mm, "end": v(-6.89, 10.74) * mm});
            skLineSegment(sketch, "E445", {"start": v(-6.89, 10.74) * mm, "end": v(-6.85, 10.65) * mm});
            skLineSegment(sketch, "E446", {"start": v(-6.85, 10.65) * mm, "end": v(-6.82, 10.57) * mm});
            skLineSegment(sketch, "E447", {"start": v(-6.82, 10.57) * mm, "end": v(-6.8, 10.5) * mm});
            skLineSegment(sketch, "E448", {"start": v(-6.8, 10.5) * mm, "end": v(-6.8, 10.43) * mm});
            skLineSegment(sketch, "E449", {"start": v(-6.8, 10.43) * mm, "end": v(-6.8, 10.38) * mm});
            skLineSegment(sketch, "E450", {"start": v(-6.8, 10.38) * mm, "end": v(-6.8, 10.32) * mm});
            skLineSegment(sketch, "E451", {"start": v(-6.8, 10.32) * mm, "end": v(-6.82, 10.27) * mm});
            skLineSegment(sketch, "E452", {"start": v(-6.82, 10.27) * mm, "end": v(-6.84, 10.23) * mm});
            skLineSegment(sketch, "E453", {"start": v(-6.84, 10.23) * mm, "end": v(-6.86, 10.18) * mm});
            skLineSegment(sketch, "E454", {"start": v(-6.86, 10.18) * mm, "end": v(-6.9, 10.14) * mm});
            skLineSegment(sketch, "E455", {"start": v(-6.9, 10.14) * mm, "end": v(-6.92, 10.1) * mm});
            skLineSegment(sketch, "E456", {"start": v(-6.92, 10.1) * mm, "end": v(-6.96, 10.06) * mm});
            skLineSegment(sketch, "E457", {"start": v(-6.96, 10.06) * mm, "end": v(-7, 10.03) * mm});
            skLineSegment(sketch, "E458", {"start": v(-7, 10.03) * mm, "end": v(-7.04, 10) * mm});
            skLineSegment(sketch, "E459", {"start": v(-7.04, 10) * mm, "end": v(-7.08, 9.97) * mm});
            skLineSegment(sketch, "E460", {"start": v(-7.08, 9.97) * mm, "end": v(-7.12, 9.94) * mm});
            skLineSegment(sketch, "E461", {"start": v(-7.12, 9.94) * mm, "end": v(-7.17, 9.92) * mm});
            skLineSegment(sketch, "E462", {"start": v(-7.17, 9.92) * mm, "end": v(-7.22, 9.9) * mm});
            skLineSegment(sketch, "E463", {"start": v(-7.22, 9.9) * mm, "end": v(-7.26, 9.9) * mm});
            skLineSegment(sketch, "E464", {"start": v(-7.26, 9.9) * mm, "end": v(-7.31, 9.89) * mm});
            skLineSegment(sketch, "E465", {"start": v(-7.31, 9.89) * mm, "end": v(-7.36, 9.89) * mm});
            skLineSegment(sketch, "E466", {"start": v(-7.36, 9.89) * mm, "end": v(-7.41, 9.89) * mm});
            skLineSegment(sketch, "E467", {"start": v(-7.41, 9.89) * mm, "end": v(-7.46, 9.89) * mm});
            skLineSegment(sketch, "E468", {"start": v(-7.46, 9.89) * mm, "end": v(-7.5, 9.9) * mm});
            skLineSegment(sketch, "E469", {"start": v(-7.5, 9.9) * mm, "end": v(-7.55, 9.9) * mm});
            skLineSegment(sketch, "E470", {"start": v(-7.55, 9.9) * mm, "end": v(-7.6, 9.92) * mm});
            skLineSegment(sketch, "E471", {"start": v(-7.6, 9.92) * mm, "end": v(-7.64, 9.94) * mm});
            skLineSegment(sketch, "E472", {"start": v(-7.64, 9.94) * mm, "end": v(-7.68, 9.96) * mm});
            skLineSegment(sketch, "E473", {"start": v(-7.68, 9.96) * mm, "end": v(-7.72, 9.99) * mm});
            skLineSegment(sketch, "E474", {"start": v(-7.72, 9.99) * mm, "end": v(-7.76, 10.02) * mm});
            skLineSegment(sketch, "E475", {"start": v(-7.76, 10.02) * mm, "end": v(-7.8, 10.06) * mm});
            skLineSegment(sketch, "E476", {"start": v(-7.8, 10.06) * mm, "end": v(-7.84, 10.1) * mm});
            skLineSegment(sketch, "E477", {"start": v(-7.84, 10.1) * mm, "end": v(-7.88, 10.16) * mm});
            skLineSegment(sketch, "E478", {"start": v(-7.88, 10.16) * mm, "end": v(-7.93, 10.22) * mm});
            skLineSegment(sketch, "E479", {"start": v(-7.93, 10.22) * mm, "end": v(-7.97, 10.28) * mm});
            skLineSegment(sketch, "E480", {"start": v(-7.97, 10.28) * mm, "end": v(-8.02, 10.35) * mm});
            skLineSegment(sketch, "E481", {"start": v(-8.02, 10.35) * mm, "end": v(-8.07, 10.43) * mm});
            skLineSegment(sketch, "E482", {"start": v(-8.07, 10.43) * mm, "end": v(-8.12, 10.5) * mm});
            skLineSegment(sketch, "E483", {"start": v(-8.12, 10.5) * mm, "end": v(-8.18, 10.59) * mm});
            skLineSegment(sketch, "E484", {"start": v(-8.18, 10.59) * mm, "end": v(-8.24, 10.67) * mm});
            skLineSegment(sketch, "E485", {"start": v(-8.24, 10.67) * mm, "end": v(-8.3, 10.76) * mm});
            skLineSegment(sketch, "E486", {"start": v(-8.3, 10.76) * mm, "end": v(-8.36, 10.86) * mm});
            skLineSegment(sketch, "E487", {"start": v(-8.36, 10.86) * mm, "end": v(-8.43, 10.95) * mm});
            skLineSegment(sketch, "E488", {"start": v(-8.43, 10.95) * mm, "end": v(-8.5, 11.04) * mm});
            skLineSegment(sketch, "E489", {"start": v(-8.5, 11.04) * mm, "end": v(-8.58, 11.13) * mm});
            skLineSegment(sketch, "E490", {"start": v(-8.58, 11.13) * mm, "end": v(-8.66, 11.22) * mm});
            skLineSegment(sketch, "E491", {"start": v(-8.66, 11.22) * mm, "end": v(-8.73, 11.3) * mm});
            skLineSegment(sketch, "E492", {"start": v(-8.73, 11.3) * mm, "end": v(-8.8, 11.39) * mm});
            skLineSegment(sketch, "E493", {"start": v(-8.8, 11.39) * mm, "end": v(-8.89, 11.46) * mm});
            skLineSegment(sketch, "E494", {"start": v(-8.89, 11.46) * mm, "end": v(-8.96, 11.53) * mm});
            skLineSegment(sketch, "E495", {"start": v(-8.96, 11.53) * mm, "end": v(-9.04, 11.6) * mm});
            skLineSegment(sketch, "E496", {"start": v(-9.04, 11.6) * mm, "end": v(-9.12, 11.65) * mm});
            skLineSegment(sketch, "E497", {"start": v(-9.12, 11.65) * mm, "end": v(-9.2, 11.7) * mm});
            skLineSegment(sketch, "E498", {"start": v(-9.2, 11.7) * mm, "end": v(-9.26, 11.75) * mm});
            skLineSegment(sketch, "E499", {"start": v(-9.26, 11.75) * mm, "end": v(-9.33, 11.79) * mm});
            skLineSegment(sketch, "E500", {"start": v(-9.33, 11.79) * mm, "end": v(-9.4, 11.82) * mm});
            skLineSegment(sketch, "E501", {"start": v(-9.4, 11.82) * mm, "end": v(-9.47, 11.85) * mm});
            skLineSegment(sketch, "E502", {"start": v(-9.47, 11.85) * mm, "end": v(-9.53, 11.87) * mm});
            skLineSegment(sketch, "E503", {"start": v(-9.53, 11.87) * mm, "end": v(-9.59, 11.88) * mm});
            skLineSegment(sketch, "E504", {"start": v(-9.59, 11.88) * mm, "end": v(-9.65, 11.9) * mm});
            skLineSegment(sketch, "E505", {"start": v(-9.65, 11.9) * mm, "end": v(-9.7, 11.9) * mm});
            skLineSegment(sketch, "E506", {"start": v(-9.7, 11.9) * mm, "end": v(-9.76, 11.9) * mm});
            skLineSegment(sketch, "E507", {"start": v(-9.76, 11.9) * mm, "end": v(-9.81, 11.9) * mm});
            skLineSegment(sketch, "E508", {"start": v(-9.81, 11.9) * mm, "end": v(-9.87, 11.89) * mm});
            skLineSegment(sketch, "E509", {"start": v(-9.87, 11.89) * mm, "end": v(-9.93, 11.88) * mm});
            skLineSegment(sketch, "E510", {"start": v(-9.93, 11.88) * mm, "end": v(-9.99, 11.87) * mm});
            skLineSegment(sketch, "E511", {"start": v(-9.99, 11.87) * mm, "end": v(-10.05, 11.85) * mm});
            skLineSegment(sketch, "E512", {"start": v(-10.05, 11.85) * mm, "end": v(-10.11, 11.83) * mm});
            skLineSegment(sketch, "E513", {"start": v(-10.11, 11.83) * mm, "end": v(-10.18, 11.81) * mm});
            skLineSegment(sketch, "E514", {"start": v(-10.18, 11.81) * mm, "end": v(-10.26, 11.78) * mm});
            skLineSegment(sketch, "E515", {"start": v(-10.26, 11.78) * mm, "end": v(-10.34, 11.75) * mm});
            skLineSegment(sketch, "E516", {"start": v(-10.34, 11.75) * mm, "end": v(-10.43, 11.7) * mm});
            skLineSegment(sketch, "E517", {"start": v(-10.43, 11.7) * mm, "end": v(-10.54, 11.66) * mm});
            skLineSegment(sketch, "E518", {"start": v(-10.54, 11.66) * mm, "end": v(-10.65, 11.61) * mm});
            skLineSegment(sketch, "E519", {"start": v(-10.65, 11.61) * mm, "end": v(-10.76, 11.56) * mm});
            skLineSegment(sketch, "E520", {"start": v(-10.76, 11.56) * mm, "end": v(-10.89, 11.5) * mm});
            skLineSegment(sketch, "E521", {"start": v(-10.89, 11.5) * mm, "end": v(-11.02, 11.44) * mm});
            skLineSegment(sketch, "E522", {"start": v(-11.02, 11.44) * mm, "end": v(-11.15, 11.38) * mm});
            skLineSegment(sketch, "E523", {"start": v(-11.15, 11.38) * mm, "end": v(-11.29, 11.31) * mm});
            skLineSegment(sketch, "E524", {"start": v(-11.29, 11.31) * mm, "end": v(-11.42, 11.25) * mm});
            skLineSegment(sketch, "E525", {"start": v(-11.42, 11.25) * mm, "end": v(-11.56, 11.2) * mm});
            skLineSegment(sketch, "E526", {"start": v(-11.56, 11.2) * mm, "end": v(-11.7, 11.13) * mm});
            skLineSegment(sketch, "E527", {"start": v(-11.7, 11.13) * mm, "end": v(-11.84, 11.08) * mm});
            skLineSegment(sketch, "E528", {"start": v(-11.84, 11.08) * mm, "end": v(-11.98, 11.02) * mm});
            skLineSegment(sketch, "E529", {"start": v(-11.98, 11.02) * mm, "end": v(-12.12, 10.97) * mm});
            skLineSegment(sketch, "E530", {"start": v(-12.12, 10.97) * mm, "end": v(-12.27, 10.92) * mm});
            skLineSegment(sketch, "E531", {"start": v(-12.27, 10.92) * mm, "end": v(-12.41, 10.87) * mm});
            skLineSegment(sketch, "E532", {"start": v(-12.41, 10.87) * mm, "end": v(-12.56, 10.82) * mm});
            skLineSegment(sketch, "E533", {"start": v(-12.56, 10.82) * mm, "end": v(-12.7, 10.78) * mm});
            skLineSegment(sketch, "E534", {"start": v(-12.7, 10.78) * mm, "end": v(-12.86, 10.74) * mm});
            skLineSegment(sketch, "E535", {"start": v(-12.86, 10.74) * mm, "end": v(-13.01, 10.7) * mm});
            skLineSegment(sketch, "E536", {"start": v(-13.01, 10.7) * mm, "end": v(-13.17, 10.67) * mm});
            skLineSegment(sketch, "E537", {"start": v(-13.17, 10.67) * mm, "end": v(-13.34, 10.64) * mm});
            skLineSegment(sketch, "E538", {"start": v(-13.34, 10.64) * mm, "end": v(-13.52, 10.6) * mm});
            skLineSegment(sketch, "E539", {"start": v(-13.52, 10.6) * mm, "end": v(-13.7, 10.58) * mm});
            skLineSegment(sketch, "E540", {"start": v(-13.7, 10.58) * mm, "end": v(-13.9, 10.55) * mm});
            skLineSegment(sketch, "E541", {"start": v(-13.9, 10.55) * mm, "end": v(-14.1, 10.52) * mm});
            skLineSegment(sketch, "E542", {"start": v(-14.1, 10.52) * mm, "end": v(-14.32, 10.5) * mm});
            skLineSegment(sketch, "E543", {"start": v(-14.32, 10.5) * mm, "end": v(-14.54, 10.48) * mm});
            skLineSegment(sketch, "E544", {"start": v(-14.54, 10.48) * mm, "end": v(-14.75, 10.46) * mm});
            skLineSegment(sketch, "E545", {"start": v(-14.75, 10.46) * mm, "end": v(-14.94, 10.44) * mm});
            skLineSegment(sketch, "E546", {"start": v(-14.94, 10.44) * mm, "end": v(-15.12, 10.43) * mm});
            skLineSegment(sketch, "E547", {"start": v(-15.12, 10.43) * mm, "end": v(-15.27, 10.42) * mm});
            skLineSegment(sketch, "E548", {"start": v(-15.27, 10.42) * mm, "end": v(-15.39, 10.42) * mm});
            skArc(sketch, "E549", {"start": v(-15.84, -13.13) * mm, "mid": v(-15.53, -13) * mm, "end": v(-15.4, -12.68) * mm});
            skArc(sketch, "E550", {"start": v(-15.4, 5.48) * mm, "mid": v(-15.53, 5.8) * mm, "end": v(-15.84, 5.92) * mm});
            skLineSegment(sketch, "E551", {"start": v(-15.4, -12.68) * mm, "end": v(-15.4, -3.7) * mm});
            skLineSegment(sketch, "E552", {"start": v(-15.4, -3.7) * mm, "end": v(-14.51, -3.7) * mm});
            skLineSegment(sketch, "E553", {"start": v(-14.51, -3.7) * mm, "end": v(-14.5, -3.85) * mm});
            skLineSegment(sketch, "E554", {"start": v(-14.5, -3.85) * mm, "end": v(-14.5, -4.05) * mm});
            skLineSegment(sketch, "E555", {"start": v(-14.5, -4.05) * mm, "end": v(-14.47, -4.19) * mm});
            skLineSegment(sketch, "E556", {"start": v(-14.47, -4.19) * mm, "end": v(-14.45, -4.29) * mm});
            skLineSegment(sketch, "E557", {"start": v(-14.45, -4.29) * mm, "end": v(-14.42, -4.35) * mm});
            skLineSegment(sketch, "E558", {"start": v(-14.42, -4.35) * mm, "end": v(-14.4, -4.39) * mm});
            skLineSegment(sketch, "E559", {"start": v(-14.4, -4.39) * mm, "end": v(-14.36, -4.41) * mm});
            skLineSegment(sketch, "E560", {"start": v(-14.36, -4.41) * mm, "end": v(-14.33, -4.43) * mm});
            skLineSegment(sketch, "E561", {"start": v(-14.33, -4.43) * mm, "end": v(-14.3, -4.45) * mm});
            skLineSegment(sketch, "E562", {"start": v(-14.3, -4.45) * mm, "end": v(-14.26, -4.47) * mm});
            skLineSegment(sketch, "E563", {"start": v(-14.26, -4.47) * mm, "end": v(-14.22, -4.48) * mm});
            skLineSegment(sketch, "E564", {"start": v(-14.22, -4.48) * mm, "end": v(-14.18, -4.5) * mm});
            skLineSegment(sketch, "E565", {"start": v(-14.18, -4.5) * mm, "end": v(-14.14, -4.5) * mm});
            skLineSegment(sketch, "E566", {"start": v(-14.14, -4.5) * mm, "end": v(-14.1, -4.5) * mm});
            skLineSegment(sketch, "E567", {"start": v(-14.1, -4.5) * mm, "end": v(-14.05, -4.5) * mm});
            skLineSegment(sketch, "E568", {"start": v(-14.05, -4.5) * mm, "end": v(-14.01, -4.5) * mm});
            skLineSegment(sketch, "E569", {"start": v(-14.01, -4.5) * mm, "end": v(-13.97, -4.5) * mm});
            skLineSegment(sketch, "E570", {"start": v(-13.97, -4.5) * mm, "end": v(-13.93, -4.48) * mm});
            skLineSegment(sketch, "E571", {"start": v(-13.93, -4.48) * mm, "end": v(-13.89, -4.47) * mm});
            skLineSegment(sketch, "E572", {"start": v(-13.89, -4.47) * mm, "end": v(-13.85, -4.46) * mm});
            skLineSegment(sketch, "E573", {"start": v(-13.85, -4.46) * mm, "end": v(-13.81, -4.44) * mm});
            skLineSegment(sketch, "E574", {"start": v(-13.81, -4.44) * mm, "end": v(-13.78, -4.42) * mm});
            skLineSegment(sketch, "E575", {"start": v(-13.78, -4.42) * mm, "end": v(-13.74, -4.4) * mm});
            skLineSegment(sketch, "E576", {"start": v(-13.74, -4.4) * mm, "end": v(-13.71, -4.37) * mm});
            skLineSegment(sketch, "E577", {"start": v(-13.71, -4.37) * mm, "end": v(-13.69, -4.34) * mm});
            skLineSegment(sketch, "E578", {"start": v(-13.69, -4.34) * mm, "end": v(-13.66, -4.28) * mm});
            skLineSegment(sketch, "E579", {"start": v(-13.66, -4.28) * mm, "end": v(-13.64, -4.2) * mm});
            skLineSegment(sketch, "E580", {"start": v(-13.64, -4.2) * mm, "end": v(-13.63, -4.1) * mm});
            skLineSegment(sketch, "E581", {"start": v(-13.63, -4.1) * mm, "end": v(-13.61, -3.94) * mm});
            skLineSegment(sketch, "E582", {"start": v(-13.61, -3.94) * mm, "end": v(-13.6, -3.74) * mm});
            skLineSegment(sketch, "E583", {"start": v(-13.6, -3.74) * mm, "end": v(-13.59, -3.48) * mm});
            skLineSegment(sketch, "E584", {"start": v(-13.59, -3.48) * mm, "end": v(-13.58, -3.16) * mm});
            skLineSegment(sketch, "E585", {"start": v(-13.58, -3.16) * mm, "end": v(-13.58, -2.79) * mm});
            skLineSegment(sketch, "E586", {"start": v(-13.58, -2.79) * mm, "end": v(-13.58, -2.36) * mm});
            skLineSegment(sketch, "E587", {"start": v(-13.58, -2.36) * mm, "end": v(-13.58, -1.9) * mm});
            skLineSegment(sketch, "E588", {"start": v(-13.58, -1.9) * mm, "end": v(-13.58, -1.4) * mm});
            skLineSegment(sketch, "E589", {"start": v(-13.58, -1.4) * mm, "end": v(-13.58, -0.87) * mm});
            skLineSegment(sketch, "E590", {"start": v(-13.58, -0.87) * mm, "end": v(-13.59, -0.33) * mm});
            skLineSegment(sketch, "E591", {"start": v(-13.59, -0.33) * mm, "end": v(-13.6, 0.23) * mm});
            skLineSegment(sketch, "E592", {"start": v(-13.6, 0.23) * mm, "end": v(-13.6, 0.8) * mm});
            skLineSegment(sketch, "E593", {"start": v(-13.6, 0.8) * mm, "end": v(-13.62, 1.35) * mm});
            skLineSegment(sketch, "E594", {"start": v(-13.62, 1.35) * mm, "end": v(-13.63, 1.9) * mm});
            skLineSegment(sketch, "E595", {"start": v(-13.63, 1.9) * mm, "end": v(-13.65, 2.45) * mm});
            skLineSegment(sketch, "E596", {"start": v(-13.65, 2.45) * mm, "end": v(-13.67, 2.97) * mm});
            skLineSegment(sketch, "E597", {"start": v(-13.67, 2.97) * mm, "end": v(-13.69, 3.46) * mm});
            skLineSegment(sketch, "E598", {"start": v(-13.69, 3.46) * mm, "end": v(-13.71, 3.92) * mm});
            skLineSegment(sketch, "E599", {"start": v(-13.71, 3.92) * mm, "end": v(-13.74, 4.35) * mm});
            skLineSegment(sketch, "E600", {"start": v(-13.74, 4.35) * mm, "end": v(-13.77, 4.73) * mm});
            skLineSegment(sketch, "E601", {"start": v(-13.77, 4.73) * mm, "end": v(-13.8, 5.07) * mm});
            skLineSegment(sketch, "E602", {"start": v(-13.8, 5.07) * mm, "end": v(-13.85, 5.37) * mm});
            skLineSegment(sketch, "E603", {"start": v(-13.85, 5.37) * mm, "end": v(-13.89, 5.64) * mm});
            skLineSegment(sketch, "E604", {"start": v(-13.89, 5.64) * mm, "end": v(-13.93, 5.87) * mm});
            skLineSegment(sketch, "E605", {"start": v(-13.93, 5.87) * mm, "end": v(-13.98, 6.08) * mm});
            skLineSegment(sketch, "E606", {"start": v(-13.98, 6.08) * mm, "end": v(-14.04, 6.27) * mm});
            skLineSegment(sketch, "E607", {"start": v(-14.04, 6.27) * mm, "end": v(-14.1, 6.43) * mm});
            skLineSegment(sketch, "E608", {"start": v(-14.1, 6.43) * mm, "end": v(-14.15, 6.58) * mm});
            skLineSegment(sketch, "E609", {"start": v(-14.15, 6.58) * mm, "end": v(-14.22, 6.7) * mm});
            skLineSegment(sketch, "E610", {"start": v(-14.22, 6.7) * mm, "end": v(-14.29, 6.82) * mm});
            skLineSegment(sketch, "E611", {"start": v(-14.29, 6.82) * mm, "end": v(-14.36, 6.93) * mm});
            skLineSegment(sketch, "E612", {"start": v(-14.36, 6.93) * mm, "end": v(-14.43, 7.02) * mm});
            skLineSegment(sketch, "E613", {"start": v(-14.43, 7.02) * mm, "end": v(-14.5, 7.1) * mm});
            skLineSegment(sketch, "E614", {"start": v(-14.5, 7.1) * mm, "end": v(-14.58, 7.16) * mm});
            skLineSegment(sketch, "E615", {"start": v(-14.58, 7.16) * mm, "end": v(-14.66, 7.22) * mm});
            skLineSegment(sketch, "E616", {"start": v(-14.66, 7.22) * mm, "end": v(-14.75, 7.28) * mm});
            skLineSegment(sketch, "E617", {"start": v(-14.75, 7.28) * mm, "end": v(-14.83, 7.32) * mm});
            skLineSegment(sketch, "E618", {"start": v(-14.83, 7.32) * mm, "end": v(-14.92, 7.36) * mm});
            skLineSegment(sketch, "E619", {"start": v(-14.92, 7.36) * mm, "end": v(-15, 7.4) * mm});
            skLineSegment(sketch, "E620", {"start": v(-15, 7.4) * mm, "end": v(-15.1, 7.42) * mm});
            skLineSegment(sketch, "E621", {"start": v(-15.1, 7.42) * mm, "end": v(-15.2, 7.44) * mm});
            skLineSegment(sketch, "E622", {"start": v(-15.2, 7.44) * mm, "end": v(-15.4, 7.47) * mm});
            skLineSegment(sketch, "E623", {"start": v(-15.4, 7.47) * mm, "end": v(-15.39, 10.42) * mm});
            skLineSegment(sketch, "E624", {"start": v(-15.74, 6.6) * mm, "end": v(-15.56, 6.6) * mm});
            skLineSegment(sketch, "E625", {"start": v(-15.56, 6.6) * mm, "end": v(-15.42, 6.59) * mm});
            skLineSegment(sketch, "E626", {"start": v(-15.42, 6.59) * mm, "end": v(-15.31, 6.57) * mm});
            skLineSegment(sketch, "E627", {"start": v(-15.31, 6.57) * mm, "end": v(-15.23, 6.55) * mm});
            skLineSegment(sketch, "E628", {"start": v(-15.23, 6.55) * mm, "end": v(-15.17, 6.53) * mm});
            skLineSegment(sketch, "E629", {"start": v(-15.17, 6.53) * mm, "end": v(-15.12, 6.5) * mm});
            skLineSegment(sketch, "E630", {"start": v(-15.12, 6.5) * mm, "end": v(-15.08, 6.47) * mm});
            skLineSegment(sketch, "E631", {"start": v(-15.08, 6.47) * mm, "end": v(-15.04, 6.44) * mm});
            skLineSegment(sketch, "E632", {"start": v(-15.04, 6.44) * mm, "end": v(-15, 6.4) * mm});
            skLineSegment(sketch, "E633", {"start": v(-15, 6.4) * mm, "end": v(-14.98, 6.37) * mm});
            skLineSegment(sketch, "E634", {"start": v(-14.98, 6.37) * mm, "end": v(-14.95, 6.32) * mm});
            skLineSegment(sketch, "E635", {"start": v(-14.95, 6.32) * mm, "end": v(-14.92, 6.27) * mm});
            skLineSegment(sketch, "E636", {"start": v(-14.92, 6.27) * mm, "end": v(-14.9, 6.22) * mm});
            skLineSegment(sketch, "E637", {"start": v(-14.9, 6.22) * mm, "end": v(-14.87, 6.16) * mm});
            skLineSegment(sketch, "E638", {"start": v(-14.87, 6.16) * mm, "end": v(-14.84, 6.1) * mm});
            skLineSegment(sketch, "E639", {"start": v(-14.84, 6.1) * mm, "end": v(-14.82, 6.01) * mm});
            skLineSegment(sketch, "E640", {"start": v(-14.82, 6.01) * mm, "end": v(-14.8, 5.93) * mm});
            skLineSegment(sketch, "E641", {"start": v(-14.8, 5.93) * mm, "end": v(-14.77, 5.82) * mm});
            skLineSegment(sketch, "E642", {"start": v(-14.77, 5.82) * mm, "end": v(-14.75, 5.7) * mm});
            skLineSegment(sketch, "E643", {"start": v(-14.75, 5.7) * mm, "end": v(-14.73, 5.54) * mm});
            skLineSegment(sketch, "E644", {"start": v(-14.73, 5.54) * mm, "end": v(-14.7, 5.35) * mm});
            skLineSegment(sketch, "E645", {"start": v(-14.7, 5.35) * mm, "end": v(-14.69, 5.13) * mm});
            skLineSegment(sketch, "E646", {"start": v(-14.69, 5.13) * mm, "end": v(-14.66, 4.87) * mm});
            skLineSegment(sketch, "E647", {"start": v(-14.66, 4.87) * mm, "end": v(-14.64, 4.57) * mm});
            skLineSegment(sketch, "E648", {"start": v(-14.64, 4.57) * mm, "end": v(-14.62, 4.22) * mm});
            skLineSegment(sketch, "E649", {"start": v(-14.62, 4.22) * mm, "end": v(-14.6, 3.83) * mm});
            skLineSegment(sketch, "E650", {"start": v(-14.6, 3.83) * mm, "end": v(-14.58, 3.4) * mm});
            skLineSegment(sketch, "E651", {"start": v(-14.58, 3.4) * mm, "end": v(-14.56, 2.93) * mm});
            skLineSegment(sketch, "E652", {"start": v(-14.56, 2.93) * mm, "end": v(-14.55, 2.42) * mm});
            skLineSegment(sketch, "E653", {"start": v(-14.55, 2.42) * mm, "end": v(-14.53, 1.88) * mm});
            skLineSegment(sketch, "E654", {"start": v(-14.53, 1.88) * mm, "end": v(-14.53, 1.3) * mm});
            skLineSegment(sketch, "E655", {"start": v(-14.53, 1.3) * mm, "end": v(-14.52, 0.7) * mm});
            skLineSegment(sketch, "E656", {"start": v(-14.52, 0.7) * mm, "end": v(-14.52, 0.07) * mm});
            skLineSegment(sketch, "E657", {"start": v(-14.52, 0.07) * mm, "end": v(-14.52, -0.57) * mm});
            skLineSegment(sketch, "E658", {"start": v(-14.52, -0.57) * mm, "end": v(-14.53, -1.18) * mm});
            skLineSegment(sketch, "E659", {"start": v(-14.53, -1.18) * mm, "end": v(-14.53, -1.78) * mm});
            skLineSegment(sketch, "E660", {"start": v(-14.53, -1.78) * mm, "end": v(-14.53, -2.33) * mm});
            skLineSegment(sketch, "E661", {"start": v(-14.53, -2.33) * mm, "end": v(-14.53, -2.82) * mm});
            skLineSegment(sketch, "E662", {"start": v(-14.53, -2.82) * mm, "end": v(-14.53, -3.28) * mm});
            skCircle(sketch, "E663", {"center": v(-27.89, 0.45) * mm, "radius": 0.8 * mm});
            skCircle(sketch, "E664", {"center": v(-28.8, 4.34) * mm, "radius": 0.8 * mm});
            skCircle(sketch, "E665", {"center": v(-31.32, 7.46) * mm, "radius": 0.8 * mm});
            skCircle(sketch, "E666", {"center": v(-34.95, 9.17) * mm, "radius": 0.8 * mm});
            skCircle(sketch, "E667", {"center": v(-38.95, 9.14) * mm, "radius": 0.8 * mm});
            skCircle(sketch, "E668", {"center": v(-42.54, 7.37) * mm, "radius": 0.8 * mm});
            skCircle(sketch, "E669", {"center": v(-45.02, 4.23) * mm, "radius": 0.8 * mm});
            skCircle(sketch, "E670", {"center": v(-45.88, 0.32) * mm, "radius": 0.8 * mm});
            skCircle(sketch, "E671", {"center": v(-44.96, -3.58) * mm, "radius": 0.8 * mm});
            skCircle(sketch, "E672", {"center": v(-42.44, -6.7) * mm, "radius": 0.8 * mm});
            skCircle(sketch, "E673", {"center": v(-38.82, -8.4) * mm, "radius": 0.8 * mm});
            skCircle(sketch, "E674", {"center": v(-34.82, -8.38) * mm, "radius": 0.8 * mm});
            skCircle(sketch, "E675", {"center": v(-31.22, -6.61) * mm, "radius": 0.8 * mm});
            skCircle(sketch, "E676", {"center": v(-28.75, -3.46) * mm, "radius": 0.8 * mm});
            skLineSegment(sketch, "E677", {"start": v(-15.95, -13.13) * mm, "end": v(-15.84, -13.13) * mm});
            skLineSegment(sketch, "E678", {"start": v(-37.93, -6.84) * mm, "end": v(-37.93, -7.36) * mm});
            skLineSegment(sketch, "E679", {"start": v(-35.84, -6.84) * mm, "end": v(-35.84, -7.36) * mm});
            skLineSegment(sketch, "E680", {"start": v(-15.4, -3.28) * mm, "end": v(-15.4, 5.48) * mm});
            skArc(sketch, "E681", {"start": v(25.28, 3.4) * mm, "mid": v(13.08, 0.38) * mm, "end": v(25.28, -2.63) * mm});
            skLineSegment(sketch, "E682", {"start": v(-37.93, -7.36) * mm, "end": v(-35.84, -7.36) * mm});
            skCircle(sketch, "E683", {"center": v(35.38, -9.48) * mm, "radius": 0.94 * mm});
            skArc(sketch, "E684", {"start": v(33.99, -8.3) * mm, "mid": v(35.38, -11.31) * mm, "end": v(36.8, -8.31) * mm});
            skArc(sketch, "E685", {"start": v(33.99, -8.3) * mm, "mid": v(34.05, -8.21) * mm, "end": v(34.09, -8.11) * mm});
            skCircle(sketch, "E686", {"center": v(35.4, -3.73) * mm, "radius": 0.94 * mm});
            skArc(sketch, "E687", {"start": v(36.8, -4.91) * mm, "mid": v(37.22, -3.5) * mm, "end": v(36.44, -2.23) * mm});
            skArc(sketch, "E688", {"start": v(34.38, -2.22) * mm, "mid": v(33.6, -3.48) * mm, "end": v(34, -4.9) * mm});
            skArc(sketch, "E689", {"start": v(34.09, -8.11) * mm, "mid": v(34.35, -6.6) * mm, "end": v(34.1, -5.1) * mm});
            skArc(sketch, "E690", {"start": v(34.1, -5.1) * mm, "mid": v(34.06, -5) * mm, "end": v(34, -4.9) * mm});
            skArc(sketch, "E691", {"start": v(36.7, -5.1) * mm, "mid": v(36.44, -6.61) * mm, "end": v(36.69, -8.12) * mm});
            skArc(sketch, "E692", {"start": v(36.69, -8.12) * mm, "mid": v(36.73, -8.22) * mm, "end": v(36.8, -8.31) * mm});
            skArc(sketch, "E693", {"start": v(36.8, -4.91) * mm, "mid": v(36.74, -5) * mm, "end": v(36.7, -5.1) * mm});
            skCircle(sketch, "E694", {"center": v(35.43, 2.01) * mm, "radius": 0.94 * mm});
            skArc(sketch, "E695", {"start": v(34.03, 3.2) * mm, "mid": v(33.61, 1.77) * mm, "end": v(34.39, 0.51) * mm});
            skArc(sketch, "E696", {"start": v(36.45, 0.5) * mm, "mid": v(37.24, 1.76) * mm, "end": v(36.83, 3.18) * mm});
            skArc(sketch, "E697", {"start": v(34.03, 3.2) * mm, "mid": v(34.09, 3.28) * mm, "end": v(34.13, 3.38) * mm});
            skCircle(sketch, "E698", {"center": v(35.45, 7.76) * mm, "radius": 0.94 * mm});
            skArc(sketch, "E699", {"start": v(36.84, 6.58) * mm, "mid": v(37.17, 7.14) * mm, "end": v(37.28, 7.78) * mm});
            skArc(sketch, "E700", {"start": v(36.1, 9.47) * mm, "mid": v(33.96, 8.82) * mm, "end": v(34.04, 6.6) * mm});
            skArc(sketch, "E701", {"start": v(34.13, 3.38) * mm, "mid": v(34.4, 4.9) * mm, "end": v(34.14, 6.4) * mm});
            skArc(sketch, "E702", {"start": v(34.14, 6.4) * mm, "mid": v(34.1, 6.5) * mm, "end": v(34.04, 6.6) * mm});
            skArc(sketch, "E703", {"start": v(36.74, 6.4) * mm, "mid": v(36.48, 4.89) * mm, "end": v(36.73, 3.37) * mm});
            skArc(sketch, "E704", {"start": v(36.73, 3.37) * mm, "mid": v(36.77, 3.27) * mm, "end": v(36.83, 3.18) * mm});
            skArc(sketch, "E705", {"start": v(36.84, 6.58) * mm, "mid": v(36.78, 6.5) * mm, "end": v(36.74, 6.4) * mm});
            skArc(sketch, "E706", {"start": v(34.38, -2.22) * mm, "mid": v(34.58, -0.86) * mm, "end": v(34.39, 0.51) * mm});
            skArc(sketch, "E707", {"start": v(36.45, 0.5) * mm, "mid": v(36.25, -0.86) * mm, "end": v(36.44, -2.23) * mm});
            skArc(sketch, "E708", {"start": v(36.1, 9.47) * mm, "mid": v(37.32, 10.1) * mm, "end": v(38.33, 11.04) * mm});
            skArc(sketch, "E709", {"start": v(39.51, 9.34) * mm, "mid": v(38.28, 8.72) * mm, "end": v(37.28, 7.78) * mm});
            skCircle(sketch, "E710", {"center": v(40.16, 11.05) * mm, "radius": 0.94 * mm});
            skArc(sketch, "E711", {"start": v(41.89, 11.65) * mm, "mid": v(39.85, 12.86) * mm, "end": v(38.33, 11.04) * mm});
            skArc(sketch, "E712", {"start": v(39.51, 9.34) * mm, "mid": v(39.98, 9.23) * mm, "end": v(40.45, 9.25) * mm});
            skArc(sketch, "E713", {"start": v(41.89, 11.65) * mm, "mid": v(41.93, 11.56) * mm, "end": v(42, 11.47) * mm});
            skCircle(sketch, "E714", {"center": v(45.1, 8.1) * mm, "radius": 0.94 * mm});
            skArc(sketch, "E715", {"start": v(43.37, 7.5) * mm, "mid": v(43.58, 7.08) * mm, "end": v(43.9, 6.72) * mm});
            skArc(sketch, "E716", {"start": v(45.96, 6.5) * mm, "mid": v(46.83, 8.7) * mm, "end": v(44.8, 9.91) * mm});
            skArc(sketch, "E717", {"start": v(43.37, 7.5) * mm, "mid": v(43.33, 7.59) * mm, "end": v(43.28, 7.66) * mm});
            skArc(sketch, "E718", {"start": v(42, 11.47) * mm, "mid": v(43.18, 10.47) * mm, "end": v(44.62, 9.92) * mm});
            skArc(sketch, "E719", {"start": v(44.62, 9.92) * mm, "mid": v(44.71, 9.9) * mm, "end": v(44.8, 9.91) * mm});
            skArc(sketch, "E720", {"start": v(43.28, 7.66) * mm, "mid": v(42.1, 8.67) * mm, "end": v(40.66, 9.24) * mm});
            skArc(sketch, "E721", {"start": v(40.66, 9.24) * mm, "mid": v(40.56, 9.25) * mm, "end": v(40.45, 9.25) * mm});
            skCircle(sketch, "E722", {"center": v(44.47, 2.4) * mm, "radius": 0.94 * mm});
            skArc(sketch, "E723", {"start": v(44.43, 0.56) * mm, "mid": v(46.17, 1.74) * mm, "end": v(45.66, 3.78) * mm});
            skArc(sketch, "E724", {"start": v(43.6, 4) * mm, "mid": v(43, 3.48) * mm, "end": v(42.67, 2.75) * mm});
            skCircle(sketch, "E725", {"center": v(39.98, -1.2) * mm, "radius": 0.94 * mm});
            skArc(sketch, "E726", {"start": v(40.02, 0.62) * mm, "mid": v(38.16, -1.33) * mm, "end": v(40.28, -3) * mm});
            skArc(sketch, "E727", {"start": v(44.25, 0.54) * mm, "mid": v(42.89, -0.21) * mm, "end": v(41.86, -1.37) * mm});
            skArc(sketch, "E728", {"start": v(44.43, 0.56) * mm, "mid": v(44.34, 0.56) * mm, "end": v(44.25, 0.53) * mm});
            skArc(sketch, "E729", {"start": v(41.86, -1.37) * mm, "mid": v(41.8, -1.47) * mm, "end": v(41.77, -1.58) * mm});
            skArc(sketch, "E730", {"start": v(40.23, 0.66) * mm, "mid": v(41.58, 1.42) * mm, "end": v(42.6, 2.58) * mm});
            skArc(sketch, "E731", {"start": v(42.6, 2.58) * mm, "mid": v(42.65, 2.66) * mm, "end": v(42.67, 2.75) * mm});
            skArc(sketch, "E732", {"start": v(40.02, 0.62) * mm, "mid": v(40.13, 0.63) * mm, "end": v(40.23, 0.66) * mm});
            skArc(sketch, "E733", {"start": v(45.96, 6.5) * mm, "mid": v(45.61, 5.16) * mm, "end": v(45.66, 3.78) * mm});
            skArc(sketch, "E734", {"start": v(43.6, 4) * mm, "mid": v(43.95, 5.34) * mm, "end": v(43.9, 6.72) * mm});
            skCircle(sketch, "E735", {"center": v(47.94, -9.5) * mm, "radius": 0.94 * mm});
            skArc(sketch, "E736", {"start": v(46.11, -9.62) * mm, "mid": v(49.2, -10.82) * mm, "end": v(48.14, -7.68) * mm});
            skArc(sketch, "E737", {"start": v(46.11, -9.62) * mm, "mid": v(46.1, -9.52) * mm, "end": v(46.05, -9.42) * mm});
            skCircle(sketch, "E738", {"center": v(43.96, -5.35) * mm, "radius": 0.94 * mm});
            skArc(sketch, "E739", {"start": v(45.78, -5.23) * mm, "mid": v(45.1, -3.92) * mm, "end": v(43.66, -3.55) * mm});
            skArc(sketch, "E740", {"start": v(42.17, -4.98) * mm, "mid": v(42.48, -6.43) * mm, "end": v(43.76, -7.17) * mm});
            skArc(sketch, "E741", {"start": v(46.05, -9.42) * mm, "mid": v(45.2, -8.15) * mm, "end": v(43.96, -7.24) * mm});
            skArc(sketch, "E742", {"start": v(43.96, -7.24) * mm, "mid": v(43.87, -7.2) * mm, "end": v(43.76, -7.17) * mm});
            skArc(sketch, "E743", {"start": v(45.84, -5.44) * mm, "mid": v(46.7, -6.7) * mm, "end": v(47.93, -7.62) * mm});
            skArc(sketch, "E744", {"start": v(47.93, -7.62) * mm, "mid": v(48.03, -7.66) * mm, "end": v(48.14, -7.68) * mm});
            skArc(sketch, "E745", {"start": v(45.78, -5.23) * mm, "mid": v(45.8, -5.34) * mm, "end": v(45.84, -5.44) * mm});
            skArc(sketch, "E746", {"start": v(42.17, -4.98) * mm, "mid": v(41.37, -3.86) * mm, "end": v(40.28, -3) * mm});
            skArc(sketch, "E747", {"start": v(41.77, -1.58) * mm, "mid": v(42.57, -2.7) * mm, "end": v(43.66, -3.55) * mm});
            skLineSegment(sketch, "E748", {"start": v(0.42, -6.9) * mm, "end": v(0.42, -7.6) * mm});
            skLineSegment(sketch, "E749", {"start": v(-0.52, -6.83) * mm, "end": v(-0.52, -7.54) * mm});
            skLineSegment(sketch, "E750", {"start": v(-15.95, 11.62) * mm, "end": v(-15.95, 11.62) * mm});
            skLineSegment(sketch, "E751", {"start": v(-17.37, -3.28) * mm, "end": v(-16.5, -3.28) * mm});
            skLineSegment(sketch, "E752", {"start": v(-15.4, -3.28) * mm, "end": v(-14.53, -3.28) * mm});
            skLineSegment(sketch, "E753.trimOffspring", {"start": v(-15.96, 6.6) * mm, "end": v(-16.16, 6.6) * mm});
            skLineSegment(sketch, "E754.trimOffspring", {"start": v(-15.95, 6.6) * mm, "end": v(-15.74, 6.6) * mm});
            skLineSegment(sketch, "E755", {"start": v(-15.96, 6.6) * mm, "end": v(-15.95, 6.6) * mm});
            skLineSegment(sketch, "E756", {"start": v(-16.06, 5.92) * mm, "end": v(-15.84, 5.92) * mm});
            skSolve(sketch);
        }
        {
            var Q0;
            Q0 = qSketchRegion(id + "F0", true);
            extrude(context, id + "F1", {"entities" : qUnion([Q0]), "depth" : 2.38 * mm, "offsetDistance" : 25.4 * mm});
        }
        {
            var Q0;
            Q0=qCreatedBy(makeId("Top.planeOp"),FACE);
            var sketch = newSketch(context, id + "F2", { "sketchPlane" : qUnion([Q0])});
            skLineSegment(sketch, "E757.bottom", {"start": v(-58.34, -15.56) * mm, "end": v(-58.34, 16.19) * mm});
            skLineSegment(sketch, "E757.top", {"start": v(52.79, -15.56) * mm, "end": v(52.79, 16.19) * mm});
            skLineSegment(sketch, "E757.left", {"start": v(-58.34, -15.56) * mm, "end": v(52.79, -15.56) * mm});
            skLineSegment(sketch, "E757.right", {"start": v(-58.34, 16.19) * mm, "end": v(52.79, 16.19) * mm});
            skLineSegment(sketch, "E758", {"start": v(52.79, 0.31) * mm, "end": v(-58.34, 0.31) * mm, "construction": true});
            skLineSegment(sketch, "E759", {"start": v(-2.77, -15.56) * mm, "end": v(-2.77, 16.19) * mm, "construction": true});
            skLineSegment(sketch, "E760", {"start": v(-55.16, 2.7) * mm, "end": v(-55.16, -2.07) * mm});
            skLineSegment(sketch, "E761", {"start": v(-51.99, 2.7) * mm, "end": v(-51.99, -2.07) * mm});
            skArc(sketch, "E762", {"start": v(-51.99, 2.7) * mm, "mid": v(-53.57, 4.28) * mm, "end": v(-55.16, 2.7) * mm});
            skArc(sketch, "E763", {"start": v(-55.16, -2.07) * mm, "mid": v(-53.57, -3.66) * mm, "end": v(-51.99, -2.07) * mm});
            skLineSegment(sketch, "E764", {"start": v(-55.16, 0.31) * mm, "end": v(-51.99, 0.31) * mm, "construction": true});
            skSolve(sketch);
        }
        {
            var Q0;
            Q0=makeQuery(id+"F2.imprint","IMPRINT",FACE,{"disambiguationData":[TD([[makeQuery(id+"F2.imprint","IMPRINT",EDGE,{"derivedFrom":sQuery(id+"F2.wireOp",EDGE,"E757.bottom")}),-1.0]])]});
            extrude(context, id + "F3", {"entities" : qUnion([Q0]), "operationType" : NewBodyOperationType.ADD, "oppositeDirection" : true, "depth" : 2.38 * mm, "offsetDistance" : 25.4 * mm});
        }
        {
            var Q0;
            Q0=makeQuery(id+"F3.opExtrude","SWEPT_EDGE",EDGE,{"disambiguationData":[OSD([sQuery(id+"F2.wireOp",EDGE,"E757.bottom"),sQuery(id+"F2.wireOp",EDGE,"E757.right")])]});
            var Q1;
            Q1=makeQuery(id+"F3.opExtrude","SWEPT_EDGE",EDGE,{"disambiguationData":[OSD([sQuery(id+"F2.wireOp",EDGE,"E757.bottom"),sQuery(id+"F2.wireOp",EDGE,"E757.left")])]});
            var Q2;
            Q2=makeQuery(id+"F3.opExtrude","SWEPT_EDGE",EDGE,{"disambiguationData":[OSD([sQuery(id+"F2.wireOp",EDGE,"E757.top"),sQuery(id+"F2.wireOp",EDGE,"E757.left")])]});
            var Q3;
            Q3=makeQuery(id+"F3.opExtrude","SWEPT_EDGE",EDGE,{"disambiguationData":[OSD([sQuery(id+"F2.wireOp",EDGE,"E757.top"),sQuery(id+"F2.wireOp",EDGE,"E757.right")])]});
            fillet(context, id + "F4", {"entities" : qUnion([Q0, Q1, Q2, Q3]), "radius" : 7.94 * mm, "tangentPropagation" : true, "allowEdgeOverflow" : false});
        }
    });
